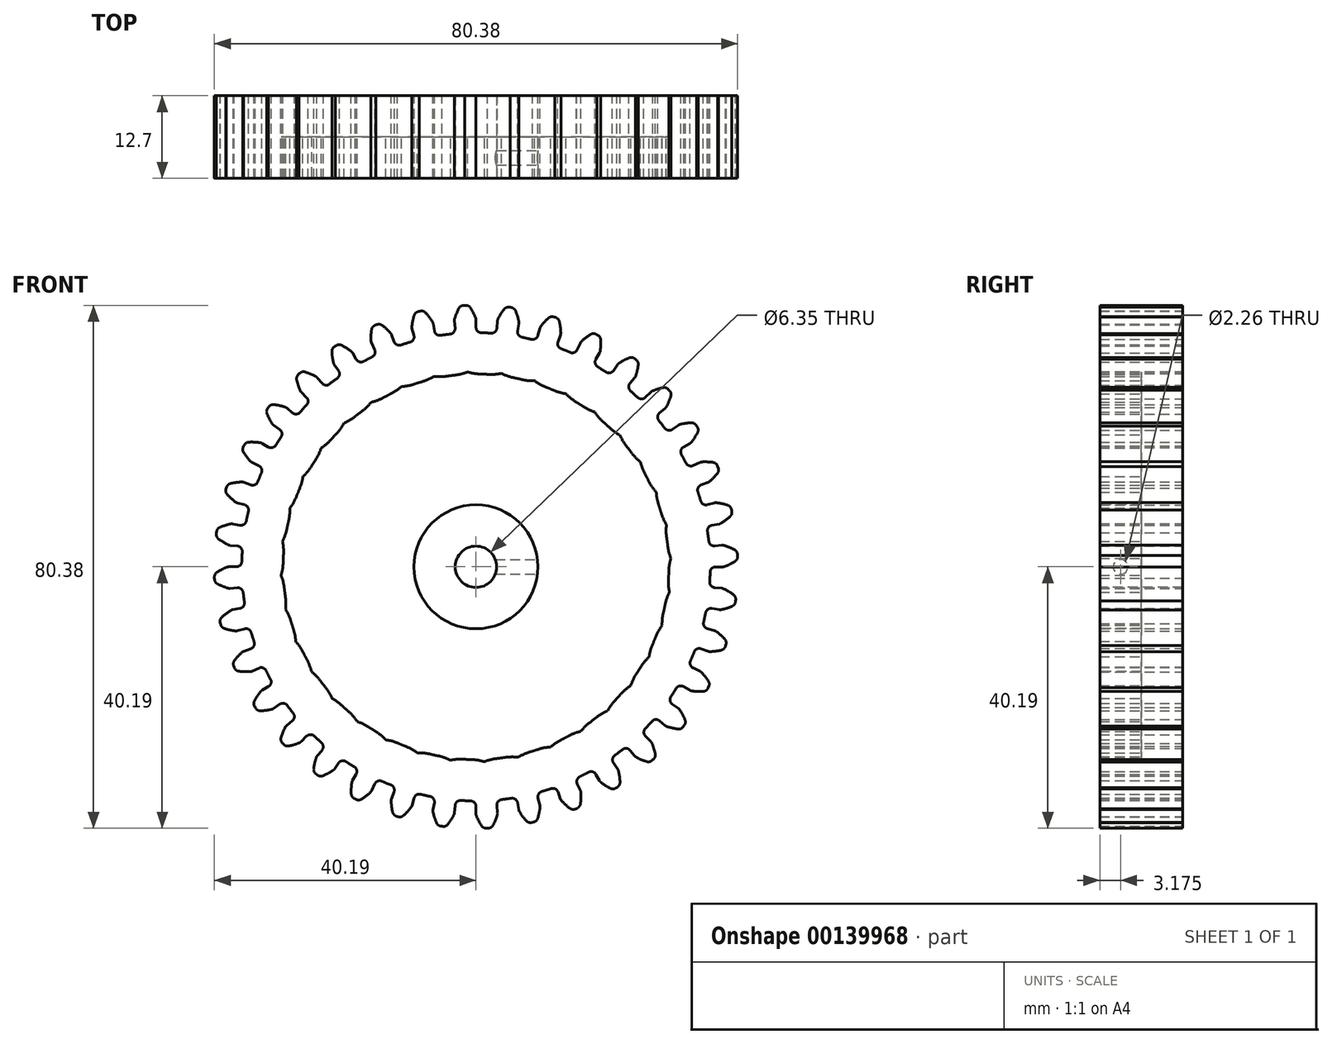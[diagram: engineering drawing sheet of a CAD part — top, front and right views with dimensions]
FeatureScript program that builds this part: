
annotation { "Feature Type Name" : "Feature", "Feature Type Description" : "" }
export const myFeature = defineFeature(function(context is Context, id is Id, definition is map)
    precondition{}
    {
        {
            var Q0;
            Q0=qCreatedBy(makeId("Front.planeOp"),FACE);
            var sketch = newSketch(context, id + "F0", { "sketchPlane" : qUnion([Q0])});
            skArc(sketch, "E0", {"start": v(-3.95, 35.77) * mm, "mid": v(-4.7, 35.68) * mm, "end": v(-5.44, 35.57) * mm});
            skArc(sketch, "E1.trimOffspring", {"start": v(-0.05, 38.26) * mm, "mid": v(-0.42, 39.05) * mm, "end": v(-0.85, 39.8) * mm});
            skLineSegment(sketch, "E2", {"start": v(0, 37.94) * mm, "end": v(0, 36.82) * mm});
            skLineSegment(sketch, "E3", {"start": v(-1.58, 40.19) * mm, "end": v(-1.75, 40.18) * mm});
            skLineSegment(sketch, "E4.MirrorCS", {"start": v(-1.93, 40.17) * mm, "end": v(-1.75, 40.18) * mm});
            skArc(sketch, "E5.MirrorCS", {"start": v(-3.28, 38.12) * mm, "mid": v(-2.99, 38.93) * mm, "end": v(-2.62, 39.72) * mm});
            skLineSegment(sketch, "E6.MirrorCS", {"start": v(-3.31, 37.8) * mm, "end": v(-3.21, 36.67) * mm});
            skPoint(sketch, "E7.visualSharp", {"position": v(-3.14, 35.85) * mm});
            skArc(sketch, "E7.filletArc", {"start": v(-3.95, 35.77) * mm, "mid": v(-3.4, 36.07) * mm, "end": v(-3.21, 36.67) * mm});
            skPoint(sketch, "E8.visualSharp", {"position": v(0, 35.98) * mm});
            skArc(sketch, "E8.filletArc", {"start": v(0, 36.82) * mm, "mid": v(0.24, 36.23) * mm, "end": v(0.82, 35.97) * mm});
            skPoint(sketch, "E9.visualSharp", {"position": v(0, 38.1) * mm});
            skArc(sketch, "E9.filletArc", {"start": v(0, 37.94) * mm, "mid": v(0, 38.1) * mm, "end": v(-0.05, 38.26) * mm});
            skPoint(sketch, "E10.visualSharp", {"position": v(-1.12, 40.2) * mm});
            skArc(sketch, "E10.filletArc", {"start": v(-0.85, 39.8) * mm, "mid": v(-1.16, 40.1) * mm, "end": v(-1.58, 40.19) * mm});
            skPoint(sketch, "E11.visualSharp", {"position": v(-3.33, 37.95) * mm});
            skArc(sketch, "E11.filletArc", {"start": v(-3.28, 38.12) * mm, "mid": v(-3.31, 37.96) * mm, "end": v(-3.31, 37.8) * mm});
            skPoint(sketch, "E12.visualSharp", {"position": v(-2.39, 40.15) * mm});
            skArc(sketch, "E12.filletArc", {"start": v(-1.93, 40.17) * mm, "mid": v(-2.34, 40.04) * mm, "end": v(-2.62, 39.72) * mm});
            skArc(sketch, "E13.1.0", {"start": v(-10.1, 34.54) * mm, "mid": v(-9.6, 34.93) * mm, "end": v(-9.53, 35.56) * mm});
            skLineSegment(sketch, "E13.1.1", {"start": v(-9.83, 36.64) * mm, "end": v(-9.53, 35.56) * mm});
            skArc(sketch, "E13.1.2", {"start": v(-9.85, 36.97) * mm, "mid": v(-9.7, 37.82) * mm, "end": v(-9.48, 38.66) * mm});
            skArc(sketch, "E13.1.3", {"start": v(-9.85, 36.97) * mm, "mid": v(-9.85, 36.8) * mm, "end": v(-9.83, 36.64) * mm});
            skArc(sketch, "E13.1.4", {"start": v(-8.88, 39.23) * mm, "mid": v(-9.25, 39.03) * mm, "end": v(-9.48, 38.66) * mm});
            skLineSegment(sketch, "E13.1.5", {"start": v(-8.53, 39.3) * mm, "end": v(-8.7, 39.27) * mm});
            skLineSegment(sketch, "E13.1.6", {"start": v(-8.88, 39.23) * mm, "end": v(-8.7, 39.27) * mm});
            skArc(sketch, "E13.1.7", {"start": v(-7.75, 39.05) * mm, "mid": v(-8.1, 39.28) * mm, "end": v(-8.53, 39.3) * mm});
            skArc(sketch, "E13.1.8", {"start": v(-6.7, 37.67) * mm, "mid": v(-7.19, 38.38) * mm, "end": v(-7.75, 39.05) * mm});
            skArc(sketch, "E13.1.9", {"start": v(-6.58, 37.36) * mm, "mid": v(-6.62, 37.52) * mm, "end": v(-6.7, 37.67) * mm});
            skLineSegment(sketch, "E13.1.10", {"start": v(-6.58, 37.36) * mm, "end": v(-6.39, 36.26) * mm});
            skArc(sketch, "E13.1.11", {"start": v(-6.39, 36.26) * mm, "mid": v(-6.05, 35.72) * mm, "end": v(-5.44, 35.57) * mm});
            skArc(sketch, "E13.2.0", {"start": v(-15.95, 32.26) * mm, "mid": v(-15.53, 32.73) * mm, "end": v(-15.56, 33.36) * mm});
            skLineSegment(sketch, "E13.2.1", {"start": v(-16.04, 34.38) * mm, "end": v(-15.56, 33.36) * mm});
            skArc(sketch, "E13.2.2", {"start": v(-16.12, 34.7) * mm, "mid": v(-16.13, 35.56) * mm, "end": v(-16.05, 36.43) * mm});
            skArc(sketch, "E13.2.3", {"start": v(-16.12, 34.7) * mm, "mid": v(-16.1, 34.53) * mm, "end": v(-16.04, 34.38) * mm});
            skArc(sketch, "E13.2.4", {"start": v(-15.55, 37.1) * mm, "mid": v(-15.89, 36.83) * mm, "end": v(-16.05, 36.43) * mm});
            skLineSegment(sketch, "E13.2.5", {"start": v(-15.23, 37.22) * mm, "end": v(-15.4, 37.16) * mm});
            skLineSegment(sketch, "E13.2.6", {"start": v(-15.55, 37.1) * mm, "end": v(-15.4, 37.16) * mm});
            skArc(sketch, "E13.2.7", {"start": v(-14.41, 37.11) * mm, "mid": v(-14.8, 37.28) * mm, "end": v(-15.23, 37.22) * mm});
            skArc(sketch, "E13.2.8", {"start": v(-13.13, 35.93) * mm, "mid": v(-13.75, 36.55) * mm, "end": v(-14.41, 37.11) * mm});
            skArc(sketch, "E13.2.9", {"start": v(-12.97, 35.65) * mm, "mid": v(-13.04, 35.8) * mm, "end": v(-13.13, 35.93) * mm});
            skLineSegment(sketch, "E13.2.10", {"start": v(-12.97, 35.65) * mm, "end": v(-12.59, 34.6) * mm});
            skArc(sketch, "E13.2.11", {"start": v(-12.59, 34.6) * mm, "mid": v(-12.16, 34.12) * mm, "end": v(-11.53, 34.09) * mm});
            skArc(sketch, "E13.3.0", {"start": v(-21.3, 29) * mm, "mid": v(-20.98, 29.54) * mm, "end": v(-21.12, 30.16) * mm});
            skLineSegment(sketch, "E13.3.1", {"start": v(-21.77, 31.07) * mm, "end": v(-21.12, 30.16) * mm});
            skArc(sketch, "E13.3.2", {"start": v(-21.9, 31.37) * mm, "mid": v(-22.06, 32.22) * mm, "end": v(-22.13, 33.09) * mm});
            skArc(sketch, "E13.3.3", {"start": v(-21.9, 31.37) * mm, "mid": v(-21.85, 31.21) * mm, "end": v(-21.77, 31.07) * mm});
            skArc(sketch, "E13.3.4", {"start": v(-21.76, 33.83) * mm, "mid": v(-22.04, 33.5) * mm, "end": v(-22.13, 33.09) * mm});
            skLineSegment(sketch, "E13.3.5", {"start": v(-21.46, 34.01) * mm, "end": v(-21.61, 33.92) * mm});
            skLineSegment(sketch, "E13.3.6", {"start": v(-21.76, 33.83) * mm, "end": v(-21.61, 33.92) * mm});
            skArc(sketch, "E13.3.7", {"start": v(-20.64, 34.04) * mm, "mid": v(-21.05, 34.14) * mm, "end": v(-21.46, 34.01) * mm});
            skArc(sketch, "E13.3.8", {"start": v(-19.17, 33.1) * mm, "mid": v(-19.88, 33.6) * mm, "end": v(-20.64, 34.04) * mm});
            skArc(sketch, "E13.3.9", {"start": v(-18.96, 32.86) * mm, "mid": v(-19.06, 33) * mm, "end": v(-19.17, 33.1) * mm});
            skLineSegment(sketch, "E13.3.10", {"start": v(-18.96, 32.86) * mm, "end": v(-18.4, 31.88) * mm});
            skArc(sketch, "E13.3.11", {"start": v(-18.4, 31.88) * mm, "mid": v(-17.9, 31.5) * mm, "end": v(-17.27, 31.57) * mm});
            skArc(sketch, "E13.4.0", {"start": v(-26.02, 24.86) * mm, "mid": v(-25.79, 25.45) * mm, "end": v(-26.03, 26.03) * mm});
            skLineSegment(sketch, "E13.4.1", {"start": v(-26.83, 26.82) * mm, "end": v(-26.03, 26.03) * mm});
            skArc(sketch, "E13.4.2", {"start": v(-27.01, 27.09) * mm, "mid": v(-27.32, 27.9) * mm, "end": v(-27.54, 28.74) * mm});
            skArc(sketch, "E13.4.3", {"start": v(-27.01, 27.09) * mm, "mid": v(-26.94, 26.95) * mm, "end": v(-26.83, 26.82) * mm});
            skArc(sketch, "E13.4.4", {"start": v(-27.3, 29.53) * mm, "mid": v(-27.53, 29.17) * mm, "end": v(-27.54, 28.74) * mm});
            skLineSegment(sketch, "E13.4.5", {"start": v(-27.04, 29.77) * mm, "end": v(-27.17, 29.65) * mm});
            skLineSegment(sketch, "E13.4.6", {"start": v(-27.3, 29.53) * mm, "end": v(-27.17, 29.65) * mm});
            skArc(sketch, "E13.4.7", {"start": v(-26.23, 29.94) * mm, "mid": v(-26.66, 29.96) * mm, "end": v(-27.04, 29.77) * mm});
            skArc(sketch, "E13.4.8", {"start": v(-24.63, 29.27) * mm, "mid": v(-25.42, 29.64) * mm, "end": v(-26.23, 29.94) * mm});
            skArc(sketch, "E13.4.9", {"start": v(-24.38, 29.07) * mm, "mid": v(-24.5, 29.18) * mm, "end": v(-24.63, 29.27) * mm});
            skLineSegment(sketch, "E13.4.10", {"start": v(-24.38, 29.07) * mm, "end": v(-23.66, 28.2) * mm});
            skArc(sketch, "E13.4.11", {"start": v(-23.66, 28.2) * mm, "mid": v(-23.1, 27.9) * mm, "end": v(-22.5, 28.09) * mm});
            skArc(sketch, "E13.5.0", {"start": v(-29.94, 19.96) * mm, "mid": v(-29.81, 20.58) * mm, "end": v(-30.16, 21.11) * mm});
            skLineSegment(sketch, "E13.5.1", {"start": v(-31.08, 21.75) * mm, "end": v(-30.16, 21.11) * mm});
            skArc(sketch, "E13.5.2", {"start": v(-31.3, 21.99) * mm, "mid": v(-31.75, 22.74) * mm, "end": v(-32.12, 23.52) * mm});
            skArc(sketch, "E13.5.3", {"start": v(-31.3, 21.99) * mm, "mid": v(-31.2, 21.86) * mm, "end": v(-31.08, 21.75) * mm});
            skArc(sketch, "E13.5.4", {"start": v(-32.01, 24.34) * mm, "mid": v(-32.17, 23.95) * mm, "end": v(-32.12, 23.52) * mm});
            skLineSegment(sketch, "E13.5.5", {"start": v(-31.8, 24.62) * mm, "end": v(-31.91, 24.49) * mm});
            skLineSegment(sketch, "E13.5.6", {"start": v(-32.01, 24.34) * mm, "end": v(-31.91, 24.49) * mm});
            skArc(sketch, "E13.5.7", {"start": v(-31.03, 24.93) * mm, "mid": v(-31.46, 24.88) * mm, "end": v(-31.8, 24.62) * mm});
            skArc(sketch, "E13.5.8", {"start": v(-29.34, 24.55) * mm, "mid": v(-30.18, 24.78) * mm, "end": v(-31.03, 24.93) * mm});
            skArc(sketch, "E13.5.9", {"start": v(-29.06, 24.4) * mm, "mid": v(-29.2, 24.49) * mm, "end": v(-29.34, 24.55) * mm});
            skLineSegment(sketch, "E13.5.10", {"start": v(-29.06, 24.4) * mm, "end": v(-28.2, 23.67) * mm});
            skArc(sketch, "E13.5.11", {"start": v(-28.2, 23.67) * mm, "mid": v(-27.6, 23.47) * mm, "end": v(-27.03, 23.75) * mm});
            skArc(sketch, "E13.6.0", {"start": v(-32.95, 14.46) * mm, "mid": v(-32.93, 15.1) * mm, "end": v(-33.37, 15.56) * mm});
            skLineSegment(sketch, "E13.6.1", {"start": v(-34.39, 16.03) * mm, "end": v(-33.37, 15.56) * mm});
            skArc(sketch, "E13.6.2", {"start": v(-34.65, 16.22) * mm, "mid": v(-35.21, 16.88) * mm, "end": v(-35.71, 17.59) * mm});
            skArc(sketch, "E13.6.3", {"start": v(-34.65, 16.22) * mm, "mid": v(-34.53, 16.1) * mm, "end": v(-34.39, 16.03) * mm});
            skArc(sketch, "E13.6.4", {"start": v(-35.76, 18.42) * mm, "mid": v(-35.84, 18) * mm, "end": v(-35.71, 17.59) * mm});
            skLineSegment(sketch, "E13.6.5", {"start": v(-35.6, 18.73) * mm, "end": v(-35.68, 18.57) * mm});
            skLineSegment(sketch, "E13.6.6", {"start": v(-35.76, 18.42) * mm, "end": v(-35.68, 18.57) * mm});
            skArc(sketch, "E13.6.7", {"start": v(-34.9, 19.17) * mm, "mid": v(-35.3, 19.04) * mm, "end": v(-35.6, 18.73) * mm});
            skArc(sketch, "E13.6.8", {"start": v(-33.16, 19.08) * mm, "mid": v(-34.02, 19.16) * mm, "end": v(-34.9, 19.17) * mm});
            skArc(sketch, "E13.6.9", {"start": v(-32.85, 18.98) * mm, "mid": v(-33, 19.04) * mm, "end": v(-33.16, 19.08) * mm});
            skLineSegment(sketch, "E13.6.10", {"start": v(-32.85, 18.98) * mm, "end": v(-31.88, 18.41) * mm});
            skArc(sketch, "E13.6.11", {"start": v(-31.88, 18.41) * mm, "mid": v(-31.25, 18.32) * mm, "end": v(-30.74, 18.7) * mm});
            skArc(sketch, "E13.7.0", {"start": v(-34.96, 8.52) * mm, "mid": v(-35.06, 9.14) * mm, "end": v(-35.56, 9.53) * mm});
            skLineSegment(sketch, "E13.7.1", {"start": v(-36.65, 9.81) * mm, "end": v(-35.56, 9.53) * mm});
            skArc(sketch, "E13.7.2", {"start": v(-36.94, 9.95) * mm, "mid": v(-37.6, 10.5) * mm, "end": v(-38.22, 11.12) * mm});
            skArc(sketch, "E13.7.3", {"start": v(-36.94, 9.95) * mm, "mid": v(-36.8, 9.87) * mm, "end": v(-36.65, 9.81) * mm});
            skArc(sketch, "E13.7.4", {"start": v(-38.41, 11.93) * mm, "mid": v(-38.42, 11.5) * mm, "end": v(-38.22, 11.12) * mm});
            skLineSegment(sketch, "E13.7.5", {"start": v(-38.3, 12.26) * mm, "end": v(-38.36, 12.1) * mm});
            skLineSegment(sketch, "E13.7.6", {"start": v(-38.41, 11.93) * mm, "end": v(-38.36, 12.1) * mm});
            skArc(sketch, "E13.7.7", {"start": v(-37.7, 12.81) * mm, "mid": v(-38.07, 12.62) * mm, "end": v(-38.3, 12.26) * mm});
            skArc(sketch, "E13.7.8", {"start": v(-35.97, 13.03) * mm, "mid": v(-36.83, 12.96) * mm, "end": v(-37.7, 12.81) * mm});
            skArc(sketch, "E13.7.9", {"start": v(-35.65, 12.98) * mm, "mid": v(-35.8, 13.02) * mm, "end": v(-35.97, 13.03) * mm});
            skLineSegment(sketch, "E13.7.10", {"start": v(-35.65, 12.98) * mm, "end": v(-34.6, 12.6) * mm});
            skArc(sketch, "E13.7.11", {"start": v(-34.6, 12.6) * mm, "mid": v(-33.96, 12.62) * mm, "end": v(-33.52, 13.08) * mm});
            skArc(sketch, "E13.8.0", {"start": v(-35.9, 2.32) * mm, "mid": v(-36.11, 2.92) * mm, "end": v(-36.68, 3.2) * mm});
            skLineSegment(sketch, "E13.8.1", {"start": v(-37.8, 3.3) * mm, "end": v(-36.68, 3.2) * mm});
            skArc(sketch, "E13.8.2", {"start": v(-38.1, 3.39) * mm, "mid": v(-38.86, 3.82) * mm, "end": v(-39.58, 4.31) * mm});
            skArc(sketch, "E13.8.3", {"start": v(-38.1, 3.39) * mm, "mid": v(-37.96, 3.33) * mm, "end": v(-37.8, 3.3) * mm});
            skArc(sketch, "E13.8.4", {"start": v(-39.9, 5.08) * mm, "mid": v(-39.84, 4.65) * mm, "end": v(-39.58, 4.31) * mm});
            skLineSegment(sketch, "E13.8.5", {"start": v(-39.85, 5.42) * mm, "end": v(-39.88, 5.25) * mm});
            skLineSegment(sketch, "E13.8.6", {"start": v(-39.9, 5.08) * mm, "end": v(-39.88, 5.25) * mm});
            skArc(sketch, "E13.8.7", {"start": v(-39.34, 6.08) * mm, "mid": v(-39.68, 5.82) * mm, "end": v(-39.85, 5.42) * mm});
            skArc(sketch, "E13.8.8", {"start": v(-37.68, 6.6) * mm, "mid": v(-38.53, 6.37) * mm, "end": v(-39.34, 6.08) * mm});
            skArc(sketch, "E13.8.9", {"start": v(-37.36, 6.6) * mm, "mid": v(-37.52, 6.6) * mm, "end": v(-37.68, 6.6) * mm});
            skLineSegment(sketch, "E13.8.10", {"start": v(-37.36, 6.6) * mm, "end": v(-36.26, 6.4) * mm});
            skArc(sketch, "E13.8.11", {"start": v(-36.26, 6.4) * mm, "mid": v(-35.64, 6.53) * mm, "end": v(-35.28, 7.06) * mm});
            skArc(sketch, "E13.9.0", {"start": v(-35.77, -3.95) * mm, "mid": v(-36.07, -3.4) * mm, "end": v(-36.67, -3.21) * mm});
            skLineSegment(sketch, "E13.9.1", {"start": v(-37.8, -3.31) * mm, "end": v(-36.67, -3.21) * mm});
            skArc(sketch, "E13.9.2", {"start": v(-38.12, -3.28) * mm, "mid": v(-38.93, -2.99) * mm, "end": v(-39.72, -2.62) * mm});
            skArc(sketch, "E13.9.3", {"start": v(-38.12, -3.28) * mm, "mid": v(-37.96, -3.31) * mm, "end": v(-37.8, -3.31) * mm});
            skArc(sketch, "E13.9.4", {"start": v(-40.17, -1.93) * mm, "mid": v(-40.04, -2.34) * mm, "end": v(-39.72, -2.62) * mm});
            skLineSegment(sketch, "E13.9.5", {"start": v(-40.19, -1.58) * mm, "end": v(-40.18, -1.75) * mm});
            skLineSegment(sketch, "E13.9.6", {"start": v(-40.17, -1.93) * mm, "end": v(-40.18, -1.75) * mm});
            skArc(sketch, "E13.9.7", {"start": v(-39.8, -0.85) * mm, "mid": v(-40.1, -1.16) * mm, "end": v(-40.19, -1.58) * mm});
            skArc(sketch, "E13.9.8", {"start": v(-38.26, -0.05) * mm, "mid": v(-39.05, -0.42) * mm, "end": v(-39.8, -0.85) * mm});
            skArc(sketch, "E13.9.9", {"start": v(-37.94, 0) * mm, "mid": v(-38.1, 0) * mm, "end": v(-38.26, -0.05) * mm});
            skLineSegment(sketch, "E13.9.10", {"start": v(-37.94, 0) * mm, "end": v(-36.82, 0) * mm});
            skArc(sketch, "E13.9.11", {"start": v(-36.82, 0) * mm, "mid": v(-36.23, 0.24) * mm, "end": v(-35.97, 0.82) * mm});
            skArc(sketch, "E13.10.0", {"start": v(-34.54, -10.1) * mm, "mid": v(-34.93, -9.6) * mm, "end": v(-35.56, -9.53) * mm});
            skLineSegment(sketch, "E13.10.1", {"start": v(-36.64, -9.83) * mm, "end": v(-35.56, -9.53) * mm});
            skArc(sketch, "E13.10.2", {"start": v(-36.97, -9.85) * mm, "mid": v(-37.82, -9.7) * mm, "end": v(-38.66, -9.48) * mm});
            skArc(sketch, "E13.10.3", {"start": v(-36.97, -9.85) * mm, "mid": v(-36.8, -9.85) * mm, "end": v(-36.64, -9.83) * mm});
            skArc(sketch, "E13.10.4", {"start": v(-39.23, -8.88) * mm, "mid": v(-39.03, -9.25) * mm, "end": v(-38.66, -9.48) * mm});
            skLineSegment(sketch, "E13.10.5", {"start": v(-39.3, -8.53) * mm, "end": v(-39.27, -8.7) * mm});
            skLineSegment(sketch, "E13.10.6", {"start": v(-39.23, -8.88) * mm, "end": v(-39.27, -8.7) * mm});
            skArc(sketch, "E13.10.7", {"start": v(-39.05, -7.75) * mm, "mid": v(-39.28, -8.1) * mm, "end": v(-39.3, -8.53) * mm});
            skArc(sketch, "E13.10.8", {"start": v(-37.67, -6.7) * mm, "mid": v(-38.38, -7.19) * mm, "end": v(-39.05, -7.75) * mm});
            skArc(sketch, "E13.10.9", {"start": v(-37.36, -6.58) * mm, "mid": v(-37.52, -6.62) * mm, "end": v(-37.67, -6.7) * mm});
            skLineSegment(sketch, "E13.10.10", {"start": v(-37.36, -6.58) * mm, "end": v(-36.26, -6.39) * mm});
            skArc(sketch, "E13.10.11", {"start": v(-36.26, -6.39) * mm, "mid": v(-35.72, -6.05) * mm, "end": v(-35.57, -5.44) * mm});
            skArc(sketch, "E13.11.0", {"start": v(-32.26, -15.95) * mm, "mid": v(-32.73, -15.53) * mm, "end": v(-33.36, -15.56) * mm});
            skLineSegment(sketch, "E13.11.1", {"start": v(-34.38, -16.04) * mm, "end": v(-33.36, -15.56) * mm});
            skArc(sketch, "E13.11.2", {"start": v(-34.7, -16.12) * mm, "mid": v(-35.56, -16.13) * mm, "end": v(-36.43, -16.05) * mm});
            skArc(sketch, "E13.11.3", {"start": v(-34.7, -16.12) * mm, "mid": v(-34.53, -16.1) * mm, "end": v(-34.38, -16.04) * mm});
            skArc(sketch, "E13.11.4", {"start": v(-37.1, -15.55) * mm, "mid": v(-36.83, -15.89) * mm, "end": v(-36.43, -16.05) * mm});
            skLineSegment(sketch, "E13.11.5", {"start": v(-37.22, -15.23) * mm, "end": v(-37.16, -15.4) * mm});
            skLineSegment(sketch, "E13.11.6", {"start": v(-37.1, -15.55) * mm, "end": v(-37.16, -15.4) * mm});
            skArc(sketch, "E13.11.7", {"start": v(-37.11, -14.41) * mm, "mid": v(-37.28, -14.8) * mm, "end": v(-37.22, -15.23) * mm});
            skArc(sketch, "E13.11.8", {"start": v(-35.93, -13.13) * mm, "mid": v(-36.55, -13.75) * mm, "end": v(-37.11, -14.41) * mm});
            skArc(sketch, "E13.11.9", {"start": v(-35.65, -12.97) * mm, "mid": v(-35.8, -13.04) * mm, "end": v(-35.93, -13.13) * mm});
            skLineSegment(sketch, "E13.11.10", {"start": v(-35.65, -12.97) * mm, "end": v(-34.6, -12.59) * mm});
            skArc(sketch, "E13.11.11", {"start": v(-34.6, -12.59) * mm, "mid": v(-34.12, -12.16) * mm, "end": v(-34.09, -11.53) * mm});
            skArc(sketch, "E13.12.0", {"start": v(-29, -21.3) * mm, "mid": v(-29.54, -20.98) * mm, "end": v(-30.16, -21.12) * mm});
            skLineSegment(sketch, "E13.12.1", {"start": v(-31.07, -21.77) * mm, "end": v(-30.16, -21.12) * mm});
            skArc(sketch, "E13.12.2", {"start": v(-31.37, -21.9) * mm, "mid": v(-32.22, -22.06) * mm, "end": v(-33.09, -22.13) * mm});
            skArc(sketch, "E13.12.3", {"start": v(-31.37, -21.9) * mm, "mid": v(-31.21, -21.85) * mm, "end": v(-31.07, -21.77) * mm});
            skArc(sketch, "E13.12.4", {"start": v(-33.83, -21.76) * mm, "mid": v(-33.5, -22.04) * mm, "end": v(-33.09, -22.13) * mm});
            skLineSegment(sketch, "E13.12.5", {"start": v(-34.01, -21.46) * mm, "end": v(-33.92, -21.61) * mm});
            skLineSegment(sketch, "E13.12.6", {"start": v(-33.83, -21.76) * mm, "end": v(-33.92, -21.61) * mm});
            skArc(sketch, "E13.12.7", {"start": v(-34.04, -20.64) * mm, "mid": v(-34.14, -21.05) * mm, "end": v(-34.01, -21.46) * mm});
            skArc(sketch, "E13.12.8", {"start": v(-33.1, -19.17) * mm, "mid": v(-33.6, -19.88) * mm, "end": v(-34.04, -20.64) * mm});
            skArc(sketch, "E13.12.9", {"start": v(-32.86, -18.96) * mm, "mid": v(-33, -19.06) * mm, "end": v(-33.1, -19.17) * mm});
            skLineSegment(sketch, "E13.12.10", {"start": v(-32.86, -18.96) * mm, "end": v(-31.88, -18.4) * mm});
            skArc(sketch, "E13.12.11", {"start": v(-31.88, -18.4) * mm, "mid": v(-31.5, -17.9) * mm, "end": v(-31.57, -17.27) * mm});
            skArc(sketch, "E13.13.0", {"start": v(-24.86, -26.02) * mm, "mid": v(-25.45, -25.79) * mm, "end": v(-26.03, -26.03) * mm});
            skLineSegment(sketch, "E13.13.1", {"start": v(-26.82, -26.83) * mm, "end": v(-26.03, -26.03) * mm});
            skArc(sketch, "E13.13.2", {"start": v(-27.09, -27.01) * mm, "mid": v(-27.9, -27.32) * mm, "end": v(-28.74, -27.54) * mm});
            skArc(sketch, "E13.13.3", {"start": v(-27.09, -27.01) * mm, "mid": v(-26.95, -26.94) * mm, "end": v(-26.82, -26.83) * mm});
            skArc(sketch, "E13.13.4", {"start": v(-29.53, -27.3) * mm, "mid": v(-29.17, -27.53) * mm, "end": v(-28.74, -27.54) * mm});
            skLineSegment(sketch, "E13.13.5", {"start": v(-29.77, -27.04) * mm, "end": v(-29.65, -27.17) * mm});
            skLineSegment(sketch, "E13.13.6", {"start": v(-29.53, -27.3) * mm, "end": v(-29.65, -27.17) * mm});
            skArc(sketch, "E13.13.7", {"start": v(-29.94, -26.23) * mm, "mid": v(-29.96, -26.66) * mm, "end": v(-29.77, -27.04) * mm});
            skArc(sketch, "E13.13.8", {"start": v(-29.27, -24.63) * mm, "mid": v(-29.64, -25.42) * mm, "end": v(-29.94, -26.23) * mm});
            skArc(sketch, "E13.13.9", {"start": v(-29.07, -24.38) * mm, "mid": v(-29.18, -24.5) * mm, "end": v(-29.27, -24.63) * mm});
            skLineSegment(sketch, "E13.13.10", {"start": v(-29.07, -24.38) * mm, "end": v(-28.2, -23.66) * mm});
            skArc(sketch, "E13.13.11", {"start": v(-28.2, -23.66) * mm, "mid": v(-27.9, -23.1) * mm, "end": v(-28.09, -22.5) * mm});
            skArc(sketch, "E13.14.0", {"start": v(-19.96, -29.94) * mm, "mid": v(-20.58, -29.81) * mm, "end": v(-21.11, -30.16) * mm});
            skLineSegment(sketch, "E13.14.1", {"start": v(-21.75, -31.08) * mm, "end": v(-21.11, -30.16) * mm});
            skArc(sketch, "E13.14.2", {"start": v(-21.99, -31.3) * mm, "mid": v(-22.74, -31.75) * mm, "end": v(-23.52, -32.12) * mm});
            skArc(sketch, "E13.14.3", {"start": v(-21.99, -31.3) * mm, "mid": v(-21.86, -31.2) * mm, "end": v(-21.75, -31.08) * mm});
            skArc(sketch, "E13.14.4", {"start": v(-24.34, -32.01) * mm, "mid": v(-23.95, -32.17) * mm, "end": v(-23.52, -32.12) * mm});
            skLineSegment(sketch, "E13.14.5", {"start": v(-24.62, -31.8) * mm, "end": v(-24.49, -31.91) * mm});
            skLineSegment(sketch, "E13.14.6", {"start": v(-24.34, -32.01) * mm, "end": v(-24.49, -31.91) * mm});
            skArc(sketch, "E13.14.7", {"start": v(-24.93, -31.03) * mm, "mid": v(-24.88, -31.46) * mm, "end": v(-24.62, -31.8) * mm});
            skArc(sketch, "E13.14.8", {"start": v(-24.55, -29.34) * mm, "mid": v(-24.78, -30.18) * mm, "end": v(-24.93, -31.03) * mm});
            skArc(sketch, "E13.14.9", {"start": v(-24.4, -29.06) * mm, "mid": v(-24.49, -29.2) * mm, "end": v(-24.55, -29.34) * mm});
            skLineSegment(sketch, "E13.14.10", {"start": v(-24.4, -29.06) * mm, "end": v(-23.67, -28.2) * mm});
            skArc(sketch, "E13.14.11", {"start": v(-23.67, -28.2) * mm, "mid": v(-23.47, -27.6) * mm, "end": v(-23.75, -27.03) * mm});
            skArc(sketch, "E13.15.0", {"start": v(-14.46, -32.95) * mm, "mid": v(-15.1, -32.93) * mm, "end": v(-15.56, -33.37) * mm});
            skLineSegment(sketch, "E13.15.1", {"start": v(-16.03, -34.39) * mm, "end": v(-15.56, -33.37) * mm});
            skArc(sketch, "E13.15.2", {"start": v(-16.22, -34.65) * mm, "mid": v(-16.88, -35.21) * mm, "end": v(-17.59, -35.71) * mm});
            skArc(sketch, "E13.15.3", {"start": v(-16.22, -34.65) * mm, "mid": v(-16.1, -34.53) * mm, "end": v(-16.03, -34.39) * mm});
            skArc(sketch, "E13.15.4", {"start": v(-18.42, -35.76) * mm, "mid": v(-18, -35.84) * mm, "end": v(-17.59, -35.71) * mm});
            skLineSegment(sketch, "E13.15.5", {"start": v(-18.73, -35.6) * mm, "end": v(-18.57, -35.68) * mm});
            skLineSegment(sketch, "E13.15.6", {"start": v(-18.42, -35.76) * mm, "end": v(-18.57, -35.68) * mm});
            skArc(sketch, "E13.15.7", {"start": v(-19.17, -34.9) * mm, "mid": v(-19.04, -35.3) * mm, "end": v(-18.73, -35.6) * mm});
            skArc(sketch, "E13.15.8", {"start": v(-19.08, -33.16) * mm, "mid": v(-19.16, -34.02) * mm, "end": v(-19.17, -34.9) * mm});
            skArc(sketch, "E13.15.9", {"start": v(-18.98, -32.85) * mm, "mid": v(-19.04, -33) * mm, "end": v(-19.08, -33.16) * mm});
            skLineSegment(sketch, "E13.15.10", {"start": v(-18.98, -32.85) * mm, "end": v(-18.41, -31.88) * mm});
            skArc(sketch, "E13.15.11", {"start": v(-18.41, -31.88) * mm, "mid": v(-18.32, -31.25) * mm, "end": v(-18.7, -30.74) * mm});
            skArc(sketch, "E13.16.0", {"start": v(-8.52, -34.96) * mm, "mid": v(-9.14, -35.06) * mm, "end": v(-9.53, -35.56) * mm});
            skLineSegment(sketch, "E13.16.1", {"start": v(-9.81, -36.65) * mm, "end": v(-9.53, -35.56) * mm});
            skArc(sketch, "E13.16.2", {"start": v(-9.95, -36.94) * mm, "mid": v(-10.5, -37.6) * mm, "end": v(-11.12, -38.22) * mm});
            skArc(sketch, "E13.16.3", {"start": v(-9.95, -36.94) * mm, "mid": v(-9.87, -36.8) * mm, "end": v(-9.81, -36.65) * mm});
            skArc(sketch, "E13.16.4", {"start": v(-11.93, -38.41) * mm, "mid": v(-11.5, -38.42) * mm, "end": v(-11.12, -38.22) * mm});
            skLineSegment(sketch, "E13.16.5", {"start": v(-12.26, -38.3) * mm, "end": v(-12.1, -38.36) * mm});
            skLineSegment(sketch, "E13.16.6", {"start": v(-11.93, -38.41) * mm, "end": v(-12.1, -38.36) * mm});
            skArc(sketch, "E13.16.7", {"start": v(-12.81, -37.7) * mm, "mid": v(-12.62, -38.07) * mm, "end": v(-12.26, -38.3) * mm});
            skArc(sketch, "E13.16.8", {"start": v(-13.03, -35.97) * mm, "mid": v(-12.96, -36.83) * mm, "end": v(-12.81, -37.7) * mm});
            skArc(sketch, "E13.16.9", {"start": v(-12.98, -35.65) * mm, "mid": v(-13.02, -35.8) * mm, "end": v(-13.03, -35.97) * mm});
            skLineSegment(sketch, "E13.16.10", {"start": v(-12.98, -35.65) * mm, "end": v(-12.6, -34.6) * mm});
            skArc(sketch, "E13.16.11", {"start": v(-12.6, -34.6) * mm, "mid": v(-12.62, -33.96) * mm, "end": v(-13.08, -33.52) * mm});
            skArc(sketch, "E13.17.0", {"start": v(-2.32, -35.9) * mm, "mid": v(-2.92, -36.11) * mm, "end": v(-3.2, -36.68) * mm});
            skLineSegment(sketch, "E13.17.1", {"start": v(-3.3, -37.8) * mm, "end": v(-3.2, -36.68) * mm});
            skArc(sketch, "E13.17.2", {"start": v(-3.39, -38.1) * mm, "mid": v(-3.82, -38.86) * mm, "end": v(-4.31, -39.58) * mm});
            skArc(sketch, "E13.17.3", {"start": v(-3.39, -38.1) * mm, "mid": v(-3.33, -37.96) * mm, "end": v(-3.3, -37.8) * mm});
            skArc(sketch, "E13.17.4", {"start": v(-5.08, -39.9) * mm, "mid": v(-4.65, -39.84) * mm, "end": v(-4.31, -39.58) * mm});
            skLineSegment(sketch, "E13.17.5", {"start": v(-5.42, -39.85) * mm, "end": v(-5.25, -39.88) * mm});
            skLineSegment(sketch, "E13.17.6", {"start": v(-5.08, -39.9) * mm, "end": v(-5.25, -39.88) * mm});
            skArc(sketch, "E13.17.7", {"start": v(-6.08, -39.34) * mm, "mid": v(-5.82, -39.68) * mm, "end": v(-5.42, -39.85) * mm});
            skArc(sketch, "E13.17.8", {"start": v(-6.6, -37.68) * mm, "mid": v(-6.37, -38.53) * mm, "end": v(-6.08, -39.34) * mm});
            skArc(sketch, "E13.17.9", {"start": v(-6.6, -37.36) * mm, "mid": v(-6.6, -37.52) * mm, "end": v(-6.6, -37.68) * mm});
            skLineSegment(sketch, "E13.17.10", {"start": v(-6.6, -37.36) * mm, "end": v(-6.4, -36.26) * mm});
            skArc(sketch, "E13.17.11", {"start": v(-6.4, -36.26) * mm, "mid": v(-6.53, -35.64) * mm, "end": v(-7.06, -35.28) * mm});
            skArc(sketch, "E13.18.0", {"start": v(3.95, -35.77) * mm, "mid": v(3.4, -36.07) * mm, "end": v(3.21, -36.67) * mm});
            skLineSegment(sketch, "E13.18.1", {"start": v(3.31, -37.8) * mm, "end": v(3.21, -36.67) * mm});
            skArc(sketch, "E13.18.2", {"start": v(3.28, -38.12) * mm, "mid": v(2.99, -38.93) * mm, "end": v(2.62, -39.72) * mm});
            skArc(sketch, "E13.18.3", {"start": v(3.28, -38.12) * mm, "mid": v(3.31, -37.96) * mm, "end": v(3.31, -37.8) * mm});
            skArc(sketch, "E13.18.4", {"start": v(1.93, -40.17) * mm, "mid": v(2.34, -40.04) * mm, "end": v(2.62, -39.72) * mm});
            skLineSegment(sketch, "E13.18.5", {"start": v(1.58, -40.19) * mm, "end": v(1.75, -40.18) * mm});
            skLineSegment(sketch, "E13.18.6", {"start": v(1.93, -40.17) * mm, "end": v(1.75, -40.18) * mm});
            skArc(sketch, "E13.18.7", {"start": v(0.85, -39.8) * mm, "mid": v(1.16, -40.1) * mm, "end": v(1.58, -40.19) * mm});
            skArc(sketch, "E13.18.8", {"start": v(0.05, -38.26) * mm, "mid": v(0.42, -39.05) * mm, "end": v(0.85, -39.8) * mm});
            skArc(sketch, "E13.18.9", {"start": v(0, -37.94) * mm, "mid": v(0, -38.1) * mm, "end": v(0.05, -38.26) * mm});
            skLineSegment(sketch, "E13.18.10", {"start": v(0, -37.94) * mm, "end": v(0, -36.82) * mm});
            skArc(sketch, "E13.18.11", {"start": v(0, -36.82) * mm, "mid": v(-0.24, -36.23) * mm, "end": v(-0.82, -35.97) * mm});
            skArc(sketch, "E13.19.0", {"start": v(10.1, -34.54) * mm, "mid": v(9.6, -34.93) * mm, "end": v(9.53, -35.56) * mm});
            skLineSegment(sketch, "E13.19.1", {"start": v(9.83, -36.64) * mm, "end": v(9.53, -35.56) * mm});
            skArc(sketch, "E13.19.2", {"start": v(9.85, -36.97) * mm, "mid": v(9.7, -37.82) * mm, "end": v(9.48, -38.66) * mm});
            skArc(sketch, "E13.19.3", {"start": v(9.85, -36.97) * mm, "mid": v(9.85, -36.8) * mm, "end": v(9.83, -36.64) * mm});
            skArc(sketch, "E13.19.4", {"start": v(8.88, -39.23) * mm, "mid": v(9.25, -39.03) * mm, "end": v(9.48, -38.66) * mm});
            skLineSegment(sketch, "E13.19.5", {"start": v(8.53, -39.3) * mm, "end": v(8.7, -39.27) * mm});
            skLineSegment(sketch, "E13.19.6", {"start": v(8.88, -39.23) * mm, "end": v(8.7, -39.27) * mm});
            skArc(sketch, "E13.19.7", {"start": v(7.75, -39.05) * mm, "mid": v(8.1, -39.28) * mm, "end": v(8.53, -39.3) * mm});
            skArc(sketch, "E13.19.8", {"start": v(6.7, -37.67) * mm, "mid": v(7.19, -38.38) * mm, "end": v(7.75, -39.05) * mm});
            skArc(sketch, "E13.19.9", {"start": v(6.58, -37.36) * mm, "mid": v(6.62, -37.52) * mm, "end": v(6.7, -37.67) * mm});
            skLineSegment(sketch, "E13.19.10", {"start": v(6.58, -37.36) * mm, "end": v(6.39, -36.26) * mm});
            skArc(sketch, "E13.19.11", {"start": v(6.39, -36.26) * mm, "mid": v(6.05, -35.72) * mm, "end": v(5.44, -35.57) * mm});
            skArc(sketch, "E13.20.0", {"start": v(15.95, -32.26) * mm, "mid": v(15.53, -32.73) * mm, "end": v(15.56, -33.36) * mm});
            skLineSegment(sketch, "E13.20.1", {"start": v(16.04, -34.38) * mm, "end": v(15.56, -33.36) * mm});
            skArc(sketch, "E13.20.2", {"start": v(16.12, -34.7) * mm, "mid": v(16.13, -35.56) * mm, "end": v(16.05, -36.43) * mm});
            skArc(sketch, "E13.20.3", {"start": v(16.12, -34.7) * mm, "mid": v(16.1, -34.53) * mm, "end": v(16.04, -34.38) * mm});
            skArc(sketch, "E13.20.4", {"start": v(15.55, -37.1) * mm, "mid": v(15.89, -36.83) * mm, "end": v(16.05, -36.43) * mm});
            skLineSegment(sketch, "E13.20.5", {"start": v(15.23, -37.22) * mm, "end": v(15.4, -37.16) * mm});
            skLineSegment(sketch, "E13.20.6", {"start": v(15.55, -37.1) * mm, "end": v(15.4, -37.16) * mm});
            skArc(sketch, "E13.20.7", {"start": v(14.41, -37.11) * mm, "mid": v(14.8, -37.28) * mm, "end": v(15.23, -37.22) * mm});
            skArc(sketch, "E13.20.8", {"start": v(13.13, -35.93) * mm, "mid": v(13.75, -36.55) * mm, "end": v(14.41, -37.11) * mm});
            skArc(sketch, "E13.20.9", {"start": v(12.97, -35.65) * mm, "mid": v(13.04, -35.8) * mm, "end": v(13.13, -35.93) * mm});
            skLineSegment(sketch, "E13.20.10", {"start": v(12.97, -35.65) * mm, "end": v(12.59, -34.6) * mm});
            skArc(sketch, "E13.20.11", {"start": v(12.59, -34.6) * mm, "mid": v(12.16, -34.12) * mm, "end": v(11.53, -34.09) * mm});
            skArc(sketch, "E13.21.0", {"start": v(21.3, -29) * mm, "mid": v(20.98, -29.54) * mm, "end": v(21.12, -30.16) * mm});
            skLineSegment(sketch, "E13.21.1", {"start": v(21.77, -31.07) * mm, "end": v(21.12, -30.16) * mm});
            skArc(sketch, "E13.21.2", {"start": v(21.9, -31.37) * mm, "mid": v(22.06, -32.22) * mm, "end": v(22.13, -33.09) * mm});
            skArc(sketch, "E13.21.3", {"start": v(21.9, -31.37) * mm, "mid": v(21.85, -31.21) * mm, "end": v(21.77, -31.07) * mm});
            skArc(sketch, "E13.21.4", {"start": v(21.76, -33.83) * mm, "mid": v(22.04, -33.5) * mm, "end": v(22.13, -33.09) * mm});
            skLineSegment(sketch, "E13.21.5", {"start": v(21.46, -34.01) * mm, "end": v(21.61, -33.92) * mm});
            skLineSegment(sketch, "E13.21.6", {"start": v(21.76, -33.83) * mm, "end": v(21.61, -33.92) * mm});
            skArc(sketch, "E13.21.7", {"start": v(20.64, -34.04) * mm, "mid": v(21.05, -34.14) * mm, "end": v(21.46, -34.01) * mm});
            skArc(sketch, "E13.21.8", {"start": v(19.17, -33.1) * mm, "mid": v(19.88, -33.6) * mm, "end": v(20.64, -34.04) * mm});
            skArc(sketch, "E13.21.9", {"start": v(18.96, -32.86) * mm, "mid": v(19.06, -33) * mm, "end": v(19.17, -33.1) * mm});
            skLineSegment(sketch, "E13.21.10", {"start": v(18.96, -32.86) * mm, "end": v(18.4, -31.88) * mm});
            skArc(sketch, "E13.21.11", {"start": v(18.4, -31.88) * mm, "mid": v(17.9, -31.5) * mm, "end": v(17.27, -31.57) * mm});
            skArc(sketch, "E13.22.0", {"start": v(26.02, -24.86) * mm, "mid": v(25.79, -25.45) * mm, "end": v(26.03, -26.03) * mm});
            skLineSegment(sketch, "E13.22.1", {"start": v(26.83, -26.82) * mm, "end": v(26.03, -26.03) * mm});
            skArc(sketch, "E13.22.2", {"start": v(27.01, -27.09) * mm, "mid": v(27.32, -27.9) * mm, "end": v(27.54, -28.74) * mm});
            skArc(sketch, "E13.22.3", {"start": v(27.01, -27.09) * mm, "mid": v(26.94, -26.95) * mm, "end": v(26.83, -26.82) * mm});
            skArc(sketch, "E13.22.4", {"start": v(27.3, -29.53) * mm, "mid": v(27.53, -29.17) * mm, "end": v(27.54, -28.74) * mm});
            skLineSegment(sketch, "E13.22.5", {"start": v(27.04, -29.77) * mm, "end": v(27.17, -29.65) * mm});
            skLineSegment(sketch, "E13.22.6", {"start": v(27.3, -29.53) * mm, "end": v(27.17, -29.65) * mm});
            skArc(sketch, "E13.22.7", {"start": v(26.23, -29.94) * mm, "mid": v(26.66, -29.96) * mm, "end": v(27.04, -29.77) * mm});
            skArc(sketch, "E13.22.8", {"start": v(24.63, -29.27) * mm, "mid": v(25.42, -29.64) * mm, "end": v(26.23, -29.94) * mm});
            skArc(sketch, "E13.22.9", {"start": v(24.38, -29.07) * mm, "mid": v(24.5, -29.18) * mm, "end": v(24.63, -29.27) * mm});
            skLineSegment(sketch, "E13.22.10", {"start": v(24.38, -29.07) * mm, "end": v(23.66, -28.2) * mm});
            skArc(sketch, "E13.22.11", {"start": v(23.66, -28.2) * mm, "mid": v(23.1, -27.9) * mm, "end": v(22.5, -28.09) * mm});
            skArc(sketch, "E13.23.0", {"start": v(29.94, -19.96) * mm, "mid": v(29.81, -20.58) * mm, "end": v(30.16, -21.11) * mm});
            skLineSegment(sketch, "E13.23.1", {"start": v(31.08, -21.75) * mm, "end": v(30.16, -21.11) * mm});
            skArc(sketch, "E13.23.2", {"start": v(31.3, -21.99) * mm, "mid": v(31.75, -22.74) * mm, "end": v(32.12, -23.52) * mm});
            skArc(sketch, "E13.23.3", {"start": v(31.3, -21.99) * mm, "mid": v(31.2, -21.86) * mm, "end": v(31.08, -21.75) * mm});
            skArc(sketch, "E13.23.4", {"start": v(32.01, -24.34) * mm, "mid": v(32.17, -23.95) * mm, "end": v(32.12, -23.52) * mm});
            skLineSegment(sketch, "E13.23.5", {"start": v(31.8, -24.62) * mm, "end": v(31.91, -24.49) * mm});
            skLineSegment(sketch, "E13.23.6", {"start": v(32.01, -24.34) * mm, "end": v(31.91, -24.49) * mm});
            skArc(sketch, "E13.23.7", {"start": v(31.03, -24.93) * mm, "mid": v(31.46, -24.88) * mm, "end": v(31.8, -24.62) * mm});
            skArc(sketch, "E13.23.8", {"start": v(29.34, -24.55) * mm, "mid": v(30.18, -24.78) * mm, "end": v(31.03, -24.93) * mm});
            skArc(sketch, "E13.23.9", {"start": v(29.06, -24.4) * mm, "mid": v(29.2, -24.49) * mm, "end": v(29.34, -24.55) * mm});
            skLineSegment(sketch, "E13.23.10", {"start": v(29.06, -24.4) * mm, "end": v(28.2, -23.67) * mm});
            skArc(sketch, "E13.23.11", {"start": v(28.2, -23.67) * mm, "mid": v(27.6, -23.47) * mm, "end": v(27.03, -23.75) * mm});
            skArc(sketch, "E13.24.0", {"start": v(32.95, -14.46) * mm, "mid": v(32.93, -15.1) * mm, "end": v(33.37, -15.56) * mm});
            skLineSegment(sketch, "E13.24.1", {"start": v(34.39, -16.03) * mm, "end": v(33.37, -15.56) * mm});
            skArc(sketch, "E13.24.2", {"start": v(34.65, -16.22) * mm, "mid": v(35.21, -16.88) * mm, "end": v(35.71, -17.59) * mm});
            skArc(sketch, "E13.24.3", {"start": v(34.65, -16.22) * mm, "mid": v(34.53, -16.1) * mm, "end": v(34.39, -16.03) * mm});
            skArc(sketch, "E13.24.4", {"start": v(35.76, -18.42) * mm, "mid": v(35.84, -18) * mm, "end": v(35.71, -17.59) * mm});
            skLineSegment(sketch, "E13.24.5", {"start": v(35.6, -18.73) * mm, "end": v(35.68, -18.57) * mm});
            skLineSegment(sketch, "E13.24.6", {"start": v(35.76, -18.42) * mm, "end": v(35.68, -18.57) * mm});
            skArc(sketch, "E13.24.7", {"start": v(34.9, -19.17) * mm, "mid": v(35.3, -19.04) * mm, "end": v(35.6, -18.73) * mm});
            skArc(sketch, "E13.24.8", {"start": v(33.16, -19.08) * mm, "mid": v(34.02, -19.16) * mm, "end": v(34.9, -19.17) * mm});
            skArc(sketch, "E13.24.9", {"start": v(32.85, -18.98) * mm, "mid": v(33, -19.04) * mm, "end": v(33.16, -19.08) * mm});
            skLineSegment(sketch, "E13.24.10", {"start": v(32.85, -18.98) * mm, "end": v(31.88, -18.41) * mm});
            skArc(sketch, "E13.24.11", {"start": v(31.88, -18.41) * mm, "mid": v(31.25, -18.32) * mm, "end": v(30.74, -18.7) * mm});
            skArc(sketch, "E13.25.0", {"start": v(34.96, -8.52) * mm, "mid": v(35.06, -9.14) * mm, "end": v(35.56, -9.53) * mm});
            skLineSegment(sketch, "E13.25.1", {"start": v(36.65, -9.81) * mm, "end": v(35.56, -9.53) * mm});
            skArc(sketch, "E13.25.2", {"start": v(36.94, -9.95) * mm, "mid": v(37.6, -10.5) * mm, "end": v(38.22, -11.12) * mm});
            skArc(sketch, "E13.25.3", {"start": v(36.94, -9.95) * mm, "mid": v(36.8, -9.87) * mm, "end": v(36.65, -9.81) * mm});
            skArc(sketch, "E13.25.4", {"start": v(38.41, -11.93) * mm, "mid": v(38.42, -11.5) * mm, "end": v(38.22, -11.12) * mm});
            skLineSegment(sketch, "E13.25.5", {"start": v(38.3, -12.26) * mm, "end": v(38.36, -12.1) * mm});
            skLineSegment(sketch, "E13.25.6", {"start": v(38.41, -11.93) * mm, "end": v(38.36, -12.1) * mm});
            skArc(sketch, "E13.25.7", {"start": v(37.7, -12.81) * mm, "mid": v(38.07, -12.62) * mm, "end": v(38.3, -12.26) * mm});
            skArc(sketch, "E13.25.8", {"start": v(35.97, -13.03) * mm, "mid": v(36.83, -12.96) * mm, "end": v(37.7, -12.81) * mm});
            skArc(sketch, "E13.25.9", {"start": v(35.65, -12.98) * mm, "mid": v(35.8, -13.02) * mm, "end": v(35.97, -13.03) * mm});
            skLineSegment(sketch, "E13.25.10", {"start": v(35.65, -12.98) * mm, "end": v(34.6, -12.6) * mm});
            skArc(sketch, "E13.25.11", {"start": v(34.6, -12.6) * mm, "mid": v(33.96, -12.62) * mm, "end": v(33.52, -13.08) * mm});
            skArc(sketch, "E13.26.0", {"start": v(35.9, -2.32) * mm, "mid": v(36.11, -2.92) * mm, "end": v(36.68, -3.2) * mm});
            skLineSegment(sketch, "E13.26.1", {"start": v(37.8, -3.3) * mm, "end": v(36.68, -3.2) * mm});
            skArc(sketch, "E13.26.2", {"start": v(38.1, -3.39) * mm, "mid": v(38.86, -3.82) * mm, "end": v(39.58, -4.31) * mm});
            skArc(sketch, "E13.26.3", {"start": v(38.1, -3.39) * mm, "mid": v(37.96, -3.33) * mm, "end": v(37.8, -3.3) * mm});
            skArc(sketch, "E13.26.4", {"start": v(39.9, -5.08) * mm, "mid": v(39.84, -4.65) * mm, "end": v(39.58, -4.31) * mm});
            skLineSegment(sketch, "E13.26.5", {"start": v(39.85, -5.42) * mm, "end": v(39.88, -5.25) * mm});
            skLineSegment(sketch, "E13.26.6", {"start": v(39.9, -5.08) * mm, "end": v(39.88, -5.25) * mm});
            skArc(sketch, "E13.26.7", {"start": v(39.34, -6.08) * mm, "mid": v(39.68, -5.82) * mm, "end": v(39.85, -5.42) * mm});
            skArc(sketch, "E13.26.8", {"start": v(37.68, -6.6) * mm, "mid": v(38.53, -6.37) * mm, "end": v(39.34, -6.08) * mm});
            skArc(sketch, "E13.26.9", {"start": v(37.36, -6.6) * mm, "mid": v(37.52, -6.6) * mm, "end": v(37.68, -6.6) * mm});
            skLineSegment(sketch, "E13.26.10", {"start": v(37.36, -6.6) * mm, "end": v(36.26, -6.4) * mm});
            skArc(sketch, "E13.26.11", {"start": v(36.26, -6.4) * mm, "mid": v(35.64, -6.53) * mm, "end": v(35.28, -7.06) * mm});
            skArc(sketch, "E13.27.0", {"start": v(35.77, 3.95) * mm, "mid": v(36.07, 3.4) * mm, "end": v(36.67, 3.21) * mm});
            skLineSegment(sketch, "E13.27.1", {"start": v(37.8, 3.31) * mm, "end": v(36.67, 3.21) * mm});
            skArc(sketch, "E13.27.2", {"start": v(38.12, 3.28) * mm, "mid": v(38.93, 2.99) * mm, "end": v(39.72, 2.62) * mm});
            skArc(sketch, "E13.27.3", {"start": v(38.12, 3.28) * mm, "mid": v(37.96, 3.31) * mm, "end": v(37.8, 3.31) * mm});
            skArc(sketch, "E13.27.4", {"start": v(40.17, 1.93) * mm, "mid": v(40.04, 2.34) * mm, "end": v(39.72, 2.62) * mm});
            skLineSegment(sketch, "E13.27.5", {"start": v(40.19, 1.58) * mm, "end": v(40.18, 1.75) * mm});
            skLineSegment(sketch, "E13.27.6", {"start": v(40.17, 1.93) * mm, "end": v(40.18, 1.75) * mm});
            skArc(sketch, "E13.27.7", {"start": v(39.8, 0.85) * mm, "mid": v(40.1, 1.16) * mm, "end": v(40.19, 1.58) * mm});
            skArc(sketch, "E13.27.8", {"start": v(38.26, 0.05) * mm, "mid": v(39.05, 0.42) * mm, "end": v(39.8, 0.85) * mm});
            skArc(sketch, "E13.27.9", {"start": v(37.94, 0) * mm, "mid": v(38.1, 0) * mm, "end": v(38.26, 0.05) * mm});
            skLineSegment(sketch, "E13.27.10", {"start": v(37.94, 0) * mm, "end": v(36.82, 0) * mm});
            skArc(sketch, "E13.27.11", {"start": v(36.82, 0) * mm, "mid": v(36.23, -0.24) * mm, "end": v(35.97, -0.82) * mm});
            skArc(sketch, "E13.28.0", {"start": v(34.54, 10.1) * mm, "mid": v(34.93, 9.6) * mm, "end": v(35.56, 9.53) * mm});
            skLineSegment(sketch, "E13.28.1", {"start": v(36.64, 9.83) * mm, "end": v(35.56, 9.53) * mm});
            skArc(sketch, "E13.28.2", {"start": v(36.97, 9.85) * mm, "mid": v(37.82, 9.7) * mm, "end": v(38.66, 9.48) * mm});
            skArc(sketch, "E13.28.3", {"start": v(36.97, 9.85) * mm, "mid": v(36.8, 9.85) * mm, "end": v(36.64, 9.83) * mm});
            skArc(sketch, "E13.28.4", {"start": v(39.23, 8.88) * mm, "mid": v(39.03, 9.25) * mm, "end": v(38.66, 9.48) * mm});
            skLineSegment(sketch, "E13.28.5", {"start": v(39.3, 8.53) * mm, "end": v(39.27, 8.7) * mm});
            skLineSegment(sketch, "E13.28.6", {"start": v(39.23, 8.88) * mm, "end": v(39.27, 8.7) * mm});
            skArc(sketch, "E13.28.7", {"start": v(39.05, 7.75) * mm, "mid": v(39.28, 8.1) * mm, "end": v(39.3, 8.53) * mm});
            skArc(sketch, "E13.28.8", {"start": v(37.67, 6.7) * mm, "mid": v(38.38, 7.19) * mm, "end": v(39.05, 7.75) * mm});
            skArc(sketch, "E13.28.9", {"start": v(37.36, 6.58) * mm, "mid": v(37.52, 6.62) * mm, "end": v(37.67, 6.7) * mm});
            skLineSegment(sketch, "E13.28.10", {"start": v(37.36, 6.58) * mm, "end": v(36.26, 6.39) * mm});
            skArc(sketch, "E13.28.11", {"start": v(36.26, 6.39) * mm, "mid": v(35.72, 6.05) * mm, "end": v(35.57, 5.44) * mm});
            skArc(sketch, "E13.29.0", {"start": v(32.26, 15.95) * mm, "mid": v(32.73, 15.53) * mm, "end": v(33.36, 15.56) * mm});
            skLineSegment(sketch, "E13.29.1", {"start": v(34.38, 16.04) * mm, "end": v(33.36, 15.56) * mm});
            skArc(sketch, "E13.29.2", {"start": v(34.7, 16.12) * mm, "mid": v(35.56, 16.13) * mm, "end": v(36.43, 16.05) * mm});
            skArc(sketch, "E13.29.3", {"start": v(34.7, 16.12) * mm, "mid": v(34.53, 16.1) * mm, "end": v(34.38, 16.04) * mm});
            skArc(sketch, "E13.29.4", {"start": v(37.1, 15.55) * mm, "mid": v(36.83, 15.89) * mm, "end": v(36.43, 16.05) * mm});
            skLineSegment(sketch, "E13.29.5", {"start": v(37.22, 15.23) * mm, "end": v(37.16, 15.4) * mm});
            skLineSegment(sketch, "E13.29.6", {"start": v(37.1, 15.55) * mm, "end": v(37.16, 15.4) * mm});
            skArc(sketch, "E13.29.7", {"start": v(37.11, 14.41) * mm, "mid": v(37.28, 14.8) * mm, "end": v(37.22, 15.23) * mm});
            skArc(sketch, "E13.29.8", {"start": v(35.93, 13.13) * mm, "mid": v(36.55, 13.75) * mm, "end": v(37.11, 14.41) * mm});
            skArc(sketch, "E13.29.9", {"start": v(35.65, 12.97) * mm, "mid": v(35.8, 13.04) * mm, "end": v(35.93, 13.13) * mm});
            skLineSegment(sketch, "E13.29.10", {"start": v(35.65, 12.97) * mm, "end": v(34.6, 12.59) * mm});
            skArc(sketch, "E13.29.11", {"start": v(34.6, 12.59) * mm, "mid": v(34.12, 12.16) * mm, "end": v(34.09, 11.53) * mm});
            skArc(sketch, "E13.30.0", {"start": v(29, 21.3) * mm, "mid": v(29.54, 20.98) * mm, "end": v(30.16, 21.12) * mm});
            skLineSegment(sketch, "E13.30.1", {"start": v(31.07, 21.77) * mm, "end": v(30.16, 21.12) * mm});
            skArc(sketch, "E13.30.2", {"start": v(31.37, 21.9) * mm, "mid": v(32.22, 22.06) * mm, "end": v(33.09, 22.13) * mm});
            skArc(sketch, "E13.30.3", {"start": v(31.37, 21.9) * mm, "mid": v(31.21, 21.85) * mm, "end": v(31.07, 21.77) * mm});
            skArc(sketch, "E13.30.4", {"start": v(33.83, 21.76) * mm, "mid": v(33.5, 22.04) * mm, "end": v(33.09, 22.13) * mm});
            skLineSegment(sketch, "E13.30.5", {"start": v(34.01, 21.46) * mm, "end": v(33.92, 21.61) * mm});
            skLineSegment(sketch, "E13.30.6", {"start": v(33.83, 21.76) * mm, "end": v(33.92, 21.61) * mm});
            skArc(sketch, "E13.30.7", {"start": v(34.04, 20.64) * mm, "mid": v(34.14, 21.05) * mm, "end": v(34.01, 21.46) * mm});
            skArc(sketch, "E13.30.8", {"start": v(33.1, 19.17) * mm, "mid": v(33.6, 19.88) * mm, "end": v(34.04, 20.64) * mm});
            skArc(sketch, "E13.30.9", {"start": v(32.86, 18.96) * mm, "mid": v(33, 19.06) * mm, "end": v(33.1, 19.17) * mm});
            skLineSegment(sketch, "E13.30.10", {"start": v(32.86, 18.96) * mm, "end": v(31.88, 18.4) * mm});
            skArc(sketch, "E13.30.11", {"start": v(31.88, 18.4) * mm, "mid": v(31.5, 17.9) * mm, "end": v(31.57, 17.27) * mm});
            skArc(sketch, "E13.31.0", {"start": v(24.86, 26.02) * mm, "mid": v(25.45, 25.79) * mm, "end": v(26.03, 26.03) * mm});
            skLineSegment(sketch, "E13.31.1", {"start": v(26.82, 26.83) * mm, "end": v(26.03, 26.03) * mm});
            skArc(sketch, "E13.31.2", {"start": v(27.09, 27.01) * mm, "mid": v(27.9, 27.32) * mm, "end": v(28.74, 27.54) * mm});
            skArc(sketch, "E13.31.3", {"start": v(27.09, 27.01) * mm, "mid": v(26.95, 26.94) * mm, "end": v(26.82, 26.83) * mm});
            skArc(sketch, "E13.31.4", {"start": v(29.53, 27.3) * mm, "mid": v(29.17, 27.53) * mm, "end": v(28.74, 27.54) * mm});
            skLineSegment(sketch, "E13.31.5", {"start": v(29.77, 27.04) * mm, "end": v(29.65, 27.17) * mm});
            skLineSegment(sketch, "E13.31.6", {"start": v(29.53, 27.3) * mm, "end": v(29.65, 27.17) * mm});
            skArc(sketch, "E13.31.7", {"start": v(29.94, 26.23) * mm, "mid": v(29.96, 26.66) * mm, "end": v(29.77, 27.04) * mm});
            skArc(sketch, "E13.31.8", {"start": v(29.27, 24.63) * mm, "mid": v(29.64, 25.42) * mm, "end": v(29.94, 26.23) * mm});
            skArc(sketch, "E13.31.9", {"start": v(29.07, 24.38) * mm, "mid": v(29.18, 24.5) * mm, "end": v(29.27, 24.63) * mm});
            skLineSegment(sketch, "E13.31.10", {"start": v(29.07, 24.38) * mm, "end": v(28.2, 23.66) * mm});
            skArc(sketch, "E13.31.11", {"start": v(28.2, 23.66) * mm, "mid": v(27.9, 23.1) * mm, "end": v(28.09, 22.5) * mm});
            skArc(sketch, "E13.32.0", {"start": v(19.96, 29.94) * mm, "mid": v(20.58, 29.81) * mm, "end": v(21.11, 30.16) * mm});
            skLineSegment(sketch, "E13.32.1", {"start": v(21.75, 31.08) * mm, "end": v(21.11, 30.16) * mm});
            skArc(sketch, "E13.32.2", {"start": v(21.99, 31.3) * mm, "mid": v(22.74, 31.75) * mm, "end": v(23.52, 32.12) * mm});
            skArc(sketch, "E13.32.3", {"start": v(21.99, 31.3) * mm, "mid": v(21.86, 31.2) * mm, "end": v(21.75, 31.08) * mm});
            skArc(sketch, "E13.32.4", {"start": v(24.34, 32.01) * mm, "mid": v(23.95, 32.17) * mm, "end": v(23.52, 32.12) * mm});
            skLineSegment(sketch, "E13.32.5", {"start": v(24.62, 31.8) * mm, "end": v(24.49, 31.91) * mm});
            skLineSegment(sketch, "E13.32.6", {"start": v(24.34, 32.01) * mm, "end": v(24.49, 31.91) * mm});
            skArc(sketch, "E13.32.7", {"start": v(24.93, 31.03) * mm, "mid": v(24.88, 31.46) * mm, "end": v(24.62, 31.8) * mm});
            skArc(sketch, "E13.32.8", {"start": v(24.55, 29.34) * mm, "mid": v(24.78, 30.18) * mm, "end": v(24.93, 31.03) * mm});
            skArc(sketch, "E13.32.9", {"start": v(24.4, 29.06) * mm, "mid": v(24.49, 29.2) * mm, "end": v(24.55, 29.34) * mm});
            skLineSegment(sketch, "E13.32.10", {"start": v(24.4, 29.06) * mm, "end": v(23.67, 28.2) * mm});
            skArc(sketch, "E13.32.11", {"start": v(23.67, 28.2) * mm, "mid": v(23.47, 27.6) * mm, "end": v(23.75, 27.03) * mm});
            skArc(sketch, "E13.33.0", {"start": v(14.46, 32.95) * mm, "mid": v(15.1, 32.93) * mm, "end": v(15.56, 33.37) * mm});
            skLineSegment(sketch, "E13.33.1", {"start": v(16.03, 34.39) * mm, "end": v(15.56, 33.37) * mm});
            skArc(sketch, "E13.33.2", {"start": v(16.22, 34.65) * mm, "mid": v(16.88, 35.21) * mm, "end": v(17.59, 35.71) * mm});
            skArc(sketch, "E13.33.3", {"start": v(16.22, 34.65) * mm, "mid": v(16.1, 34.53) * mm, "end": v(16.03, 34.39) * mm});
            skArc(sketch, "E13.33.4", {"start": v(18.42, 35.76) * mm, "mid": v(18, 35.84) * mm, "end": v(17.59, 35.71) * mm});
            skLineSegment(sketch, "E13.33.5", {"start": v(18.73, 35.6) * mm, "end": v(18.57, 35.68) * mm});
            skLineSegment(sketch, "E13.33.6", {"start": v(18.42, 35.76) * mm, "end": v(18.57, 35.68) * mm});
            skArc(sketch, "E13.33.7", {"start": v(19.17, 34.9) * mm, "mid": v(19.04, 35.3) * mm, "end": v(18.73, 35.6) * mm});
            skArc(sketch, "E13.33.8", {"start": v(19.08, 33.16) * mm, "mid": v(19.16, 34.02) * mm, "end": v(19.17, 34.9) * mm});
            skArc(sketch, "E13.33.9", {"start": v(18.98, 32.85) * mm, "mid": v(19.04, 33) * mm, "end": v(19.08, 33.16) * mm});
            skLineSegment(sketch, "E13.33.10", {"start": v(18.98, 32.85) * mm, "end": v(18.41, 31.88) * mm});
            skArc(sketch, "E13.33.11", {"start": v(18.41, 31.88) * mm, "mid": v(18.32, 31.25) * mm, "end": v(18.7, 30.74) * mm});
            skArc(sketch, "E13.34.0", {"start": v(8.52, 34.96) * mm, "mid": v(9.14, 35.06) * mm, "end": v(9.53, 35.56) * mm});
            skLineSegment(sketch, "E13.34.1", {"start": v(9.81, 36.65) * mm, "end": v(9.53, 35.56) * mm});
            skArc(sketch, "E13.34.2", {"start": v(9.95, 36.94) * mm, "mid": v(10.5, 37.6) * mm, "end": v(11.12, 38.22) * mm});
            skArc(sketch, "E13.34.3", {"start": v(9.95, 36.94) * mm, "mid": v(9.87, 36.8) * mm, "end": v(9.81, 36.65) * mm});
            skArc(sketch, "E13.34.4", {"start": v(11.93, 38.41) * mm, "mid": v(11.5, 38.42) * mm, "end": v(11.12, 38.22) * mm});
            skLineSegment(sketch, "E13.34.5", {"start": v(12.26, 38.3) * mm, "end": v(12.1, 38.36) * mm});
            skLineSegment(sketch, "E13.34.6", {"start": v(11.93, 38.41) * mm, "end": v(12.1, 38.36) * mm});
            skArc(sketch, "E13.34.7", {"start": v(12.81, 37.7) * mm, "mid": v(12.62, 38.07) * mm, "end": v(12.26, 38.3) * mm});
            skArc(sketch, "E13.34.8", {"start": v(13.03, 35.97) * mm, "mid": v(12.96, 36.83) * mm, "end": v(12.81, 37.7) * mm});
            skArc(sketch, "E13.34.9", {"start": v(12.98, 35.65) * mm, "mid": v(13.02, 35.8) * mm, "end": v(13.03, 35.97) * mm});
            skLineSegment(sketch, "E13.34.10", {"start": v(12.98, 35.65) * mm, "end": v(12.6, 34.6) * mm});
            skArc(sketch, "E13.34.11", {"start": v(12.6, 34.6) * mm, "mid": v(12.62, 33.96) * mm, "end": v(13.08, 33.52) * mm});
            skArc(sketch, "E13.35.0", {"start": v(2.32, 35.9) * mm, "mid": v(2.92, 36.11) * mm, "end": v(3.2, 36.68) * mm});
            skLineSegment(sketch, "E13.35.1", {"start": v(3.3, 37.8) * mm, "end": v(3.2, 36.68) * mm});
            skArc(sketch, "E13.35.2", {"start": v(3.39, 38.1) * mm, "mid": v(3.82, 38.86) * mm, "end": v(4.31, 39.58) * mm});
            skArc(sketch, "E13.35.3", {"start": v(3.39, 38.1) * mm, "mid": v(3.33, 37.96) * mm, "end": v(3.3, 37.8) * mm});
            skArc(sketch, "E13.35.4", {"start": v(5.08, 39.9) * mm, "mid": v(4.65, 39.84) * mm, "end": v(4.31, 39.58) * mm});
            skLineSegment(sketch, "E13.35.5", {"start": v(5.42, 39.85) * mm, "end": v(5.25, 39.88) * mm});
            skLineSegment(sketch, "E13.35.6", {"start": v(5.08, 39.9) * mm, "end": v(5.25, 39.88) * mm});
            skArc(sketch, "E13.35.7", {"start": v(6.08, 39.34) * mm, "mid": v(5.82, 39.68) * mm, "end": v(5.42, 39.85) * mm});
            skArc(sketch, "E13.35.8", {"start": v(6.6, 37.68) * mm, "mid": v(6.37, 38.53) * mm, "end": v(6.08, 39.34) * mm});
            skArc(sketch, "E13.35.9", {"start": v(6.6, 37.36) * mm, "mid": v(6.6, 37.52) * mm, "end": v(6.6, 37.68) * mm});
            skLineSegment(sketch, "E13.35.10", {"start": v(6.6, 37.36) * mm, "end": v(6.4, 36.26) * mm});
            skArc(sketch, "E13.35.11", {"start": v(6.4, 36.26) * mm, "mid": v(6.53, 35.64) * mm, "end": v(7.06, 35.28) * mm});
            skArc(sketch, "E14.trimOffspring", {"start": v(2.32, 35.9) * mm, "mid": v(1.57, 35.95) * mm, "end": v(0.82, 35.97) * mm});
            skArc(sketch, "E15.trimOffspring", {"start": v(8.52, 34.96) * mm, "mid": v(7.79, 35.13) * mm, "end": v(7.06, 35.28) * mm});
            skArc(sketch, "E16.trimOffspring", {"start": v(14.46, 32.95) * mm, "mid": v(13.77, 33.24) * mm, "end": v(13.08, 33.52) * mm});
            skArc(sketch, "E17.trimOffspring", {"start": v(-32.95, 14.46) * mm, "mid": v(-33.24, 13.77) * mm, "end": v(-33.52, 13.08) * mm});
            skArc(sketch, "E18.trimOffspring", {"start": v(-29.94, 19.96) * mm, "mid": v(-30.35, 19.33) * mm, "end": v(-30.74, 18.7) * mm});
            skArc(sketch, "E19.trimOffspring", {"start": v(-26.02, 24.86) * mm, "mid": v(-26.53, 24.3) * mm, "end": v(-27.03, 23.75) * mm});
            skArc(sketch, "E20.trimOffspring", {"start": v(-21.3, 29) * mm, "mid": v(-21.9, 28.55) * mm, "end": v(-22.5, 28.09) * mm});
            skArc(sketch, "E21.trimOffspring", {"start": v(-10.1, 34.54) * mm, "mid": v(-10.82, 34.32) * mm, "end": v(-11.53, 34.09) * mm});
            skArc(sketch, "E22.trimOffspring", {"start": v(-15.95, 32.26) * mm, "mid": v(-16.62, 31.92) * mm, "end": v(-17.27, 31.57) * mm});
            skArc(sketch, "E23.trimOffspring", {"start": v(-34.96, 8.52) * mm, "mid": v(-35.13, 7.79) * mm, "end": v(-35.28, 7.06) * mm});
            skArc(sketch, "E24.trimOffspring", {"start": v(-35.9, 2.32) * mm, "mid": v(-35.95, 1.57) * mm, "end": v(-35.97, 0.82) * mm});
            skArc(sketch, "E25.trimOffspring", {"start": v(-35.77, -3.95) * mm, "mid": v(-35.68, -4.7) * mm, "end": v(-35.57, -5.44) * mm});
            skArc(sketch, "E26.trimOffspring", {"start": v(-34.54, -10.1) * mm, "mid": v(-34.32, -10.82) * mm, "end": v(-34.09, -11.53) * mm});
            skArc(sketch, "E27.trimOffspring", {"start": v(-32.26, -15.95) * mm, "mid": v(-31.92, -16.62) * mm, "end": v(-31.57, -17.27) * mm});
            skArc(sketch, "E28.trimOffspring", {"start": v(19.96, 29.94) * mm, "mid": v(19.33, 30.35) * mm, "end": v(18.7, 30.74) * mm});
            skArc(sketch, "E29.trimOffspring", {"start": v(24.86, 26.02) * mm, "mid": v(24.3, 26.53) * mm, "end": v(23.75, 27.03) * mm});
            skArc(sketch, "E30.trimOffspring", {"start": v(29, 21.3) * mm, "mid": v(28.55, 21.9) * mm, "end": v(28.09, 22.5) * mm});
            skArc(sketch, "E31.trimOffspring", {"start": v(32.26, 15.95) * mm, "mid": v(31.92, 16.62) * mm, "end": v(31.57, 17.27) * mm});
            skArc(sketch, "E32.trimOffspring", {"start": v(34.54, 10.1) * mm, "mid": v(34.32, 10.82) * mm, "end": v(34.09, 11.53) * mm});
            skArc(sketch, "E33.trimOffspring", {"start": v(35.77, 3.95) * mm, "mid": v(35.68, 4.7) * mm, "end": v(35.57, 5.44) * mm});
            skArc(sketch, "E34.trimOffspring", {"start": v(35.9, -2.32) * mm, "mid": v(35.95, -1.57) * mm, "end": v(35.97, -0.82) * mm});
            skArc(sketch, "E35.trimOffspring", {"start": v(34.96, -8.52) * mm, "mid": v(35.13, -7.79) * mm, "end": v(35.28, -7.06) * mm});
            skArc(sketch, "E36.trimOffspring", {"start": v(32.95, -14.46) * mm, "mid": v(33.24, -13.77) * mm, "end": v(33.52, -13.08) * mm});
            skArc(sketch, "E37.trimOffspring", {"start": v(29.94, -19.96) * mm, "mid": v(30.35, -19.33) * mm, "end": v(30.74, -18.7) * mm});
            skArc(sketch, "E38.trimOffspring", {"start": v(26.02, -24.86) * mm, "mid": v(26.53, -24.3) * mm, "end": v(27.03, -23.75) * mm});
            skArc(sketch, "E39.trimOffspring", {"start": v(21.3, -29) * mm, "mid": v(21.9, -28.55) * mm, "end": v(22.5, -28.09) * mm});
            skArc(sketch, "E40.trimOffspring", {"start": v(15.95, -32.26) * mm, "mid": v(16.62, -31.92) * mm, "end": v(17.27, -31.57) * mm});
            skArc(sketch, "E41.trimOffspring", {"start": v(-2.32, -35.9) * mm, "mid": v(-1.57, -35.95) * mm, "end": v(-0.82, -35.97) * mm});
            skArc(sketch, "E42.trimOffspring", {"start": v(-8.52, -34.96) * mm, "mid": v(-7.79, -35.13) * mm, "end": v(-7.06, -35.28) * mm});
            skArc(sketch, "E43.trimOffspring", {"start": v(-14.46, -32.95) * mm, "mid": v(-13.77, -33.24) * mm, "end": v(-13.08, -33.52) * mm});
            skArc(sketch, "E44.trimOffspring", {"start": v(-19.96, -29.94) * mm, "mid": v(-19.33, -30.35) * mm, "end": v(-18.7, -30.74) * mm});
            skArc(sketch, "E45.trimOffspring", {"start": v(-24.86, -26.02) * mm, "mid": v(-24.3, -26.53) * mm, "end": v(-23.75, -27.03) * mm});
            skArc(sketch, "E46.trimOffspring", {"start": v(-29, -21.3) * mm, "mid": v(-28.55, -21.9) * mm, "end": v(-28.09, -22.5) * mm});
            skArc(sketch, "E47.trimOffspring", {"start": v(3.95, -35.77) * mm, "mid": v(4.7, -35.68) * mm, "end": v(5.44, -35.57) * mm});
            skArc(sketch, "E48.trimOffspring", {"start": v(10.1, -34.54) * mm, "mid": v(10.82, -34.32) * mm, "end": v(11.53, -34.09) * mm});
            skSolve(sketch);
        }
        {
            var Q0;
            Q0 = qSketchRegion(id + "F0", true);
            extrude(context, id + "F1", {"entities" : qUnion([Q0]), "depth" : 12.7 * mm});
        }
        {
            var Q0;
            Q0=makeQuery(id+"F1.opExtrude","CAP_FACE",FACE,{"disambiguationData":[OSD([sQuery(id+"F0.wireOp",EDGE,"E0"),sQuery(id+"F0.wireOp",EDGE,"E1.trimOffspring"),sQuery(id+"F0.wireOp",EDGE,"E2"),sQuery(id+"F0.wireOp",EDGE,"E3"),sQuery(id+"F0.wireOp",EDGE,"E4.MirrorCS"),sQuery(id+"F0.wireOp",EDGE,"E5.MirrorCS"),sQuery(id+"F0.wireOp",EDGE,"E6.MirrorCS"),sQuery(id+"F0.wireOp",EDGE,"E7.filletArc"),sQuery(id+"F0.wireOp",EDGE,"E8.filletArc"),sQuery(id+"F0.wireOp",EDGE,"E9.filletArc"),sQuery(id+"F0.wireOp",EDGE,"E10.filletArc"),sQuery(id+"F0.wireOp",EDGE,"E11.filletArc"),sQuery(id+"F0.wireOp",EDGE,"E12.filletArc"),sQuery(id+"F0.wireOp",EDGE,"E13.1.0"),sQuery(id+"F0.wireOp",EDGE,"E13.1.1"),sQuery(id+"F0.wireOp",EDGE,"E13.1.2"),sQuery(id+"F0.wireOp",EDGE,"E13.1.3"),sQuery(id+"F0.wireOp",EDGE,"E13.1.4"),sQuery(id+"F0.wireOp",EDGE,"E13.1.5"),sQuery(id+"F0.wireOp",EDGE,"E13.1.6"),sQuery(id+"F0.wireOp",EDGE,"E13.1.7"),sQuery(id+"F0.wireOp",EDGE,"E13.1.8"),sQuery(id+"F0.wireOp",EDGE,"E13.1.9"),sQuery(id+"F0.wireOp",EDGE,"E13.1.10"),sQuery(id+"F0.wireOp",EDGE,"E13.1.11"),sQuery(id+"F0.wireOp",EDGE,"E13.2.0"),sQuery(id+"F0.wireOp",EDGE,"E13.2.1"),sQuery(id+"F0.wireOp",EDGE,"E13.2.2"),sQuery(id+"F0.wireOp",EDGE,"E13.2.3"),sQuery(id+"F0.wireOp",EDGE,"E13.2.4"),sQuery(id+"F0.wireOp",EDGE,"E13.2.5"),sQuery(id+"F0.wireOp",EDGE,"E13.2.6"),sQuery(id+"F0.wireOp",EDGE,"E13.2.7"),sQuery(id+"F0.wireOp",EDGE,"E13.2.8"),sQuery(id+"F0.wireOp",EDGE,"E13.2.9"),sQuery(id+"F0.wireOp",EDGE,"E13.2.10"),sQuery(id+"F0.wireOp",EDGE,"E13.2.11"),sQuery(id+"F0.wireOp",EDGE,"E13.3.0"),sQuery(id+"F0.wireOp",EDGE,"E13.3.1"),sQuery(id+"F0.wireOp",EDGE,"E13.3.2"),sQuery(id+"F0.wireOp",EDGE,"E13.3.3"),sQuery(id+"F0.wireOp",EDGE,"E13.3.4"),sQuery(id+"F0.wireOp",EDGE,"E13.3.5"),sQuery(id+"F0.wireOp",EDGE,"E13.3.6"),sQuery(id+"F0.wireOp",EDGE,"E13.3.7"),sQuery(id+"F0.wireOp",EDGE,"E13.3.8"),sQuery(id+"F0.wireOp",EDGE,"E13.3.9"),sQuery(id+"F0.wireOp",EDGE,"E13.3.10"),sQuery(id+"F0.wireOp",EDGE,"E13.3.11"),sQuery(id+"F0.wireOp",EDGE,"E13.4.0"),sQuery(id+"F0.wireOp",EDGE,"E13.4.1"),sQuery(id+"F0.wireOp",EDGE,"E13.4.2"),sQuery(id+"F0.wireOp",EDGE,"E13.4.3"),sQuery(id+"F0.wireOp",EDGE,"E13.4.4"),sQuery(id+"F0.wireOp",EDGE,"E13.4.5"),sQuery(id+"F0.wireOp",EDGE,"E13.4.6"),sQuery(id+"F0.wireOp",EDGE,"E13.4.7"),sQuery(id+"F0.wireOp",EDGE,"E13.4.8"),sQuery(id+"F0.wireOp",EDGE,"E13.4.9"),sQuery(id+"F0.wireOp",EDGE,"E13.4.10"),sQuery(id+"F0.wireOp",EDGE,"E13.4.11"),sQuery(id+"F0.wireOp",EDGE,"E13.5.0"),sQuery(id+"F0.wireOp",EDGE,"E13.5.1"),sQuery(id+"F0.wireOp",EDGE,"E13.5.2"),sQuery(id+"F0.wireOp",EDGE,"E13.5.3"),sQuery(id+"F0.wireOp",EDGE,"E13.5.4"),sQuery(id+"F0.wireOp",EDGE,"E13.5.5"),sQuery(id+"F0.wireOp",EDGE,"E13.5.6"),sQuery(id+"F0.wireOp",EDGE,"E13.5.7"),sQuery(id+"F0.wireOp",EDGE,"E13.5.8"),sQuery(id+"F0.wireOp",EDGE,"E13.5.9"),sQuery(id+"F0.wireOp",EDGE,"E13.5.10"),sQuery(id+"F0.wireOp",EDGE,"E13.5.11"),sQuery(id+"F0.wireOp",EDGE,"E13.6.0"),sQuery(id+"F0.wireOp",EDGE,"E13.6.1"),sQuery(id+"F0.wireOp",EDGE,"E13.6.2"),sQuery(id+"F0.wireOp",EDGE,"E13.6.3"),sQuery(id+"F0.wireOp",EDGE,"E13.6.4"),sQuery(id+"F0.wireOp",EDGE,"E13.6.5"),sQuery(id+"F0.wireOp",EDGE,"E13.6.6"),sQuery(id+"F0.wireOp",EDGE,"E13.6.7"),sQuery(id+"F0.wireOp",EDGE,"E13.6.8"),sQuery(id+"F0.wireOp",EDGE,"E13.6.9"),sQuery(id+"F0.wireOp",EDGE,"E13.6.10"),sQuery(id+"F0.wireOp",EDGE,"E13.6.11"),sQuery(id+"F0.wireOp",EDGE,"E13.7.0"),sQuery(id+"F0.wireOp",EDGE,"E13.7.1"),sQuery(id+"F0.wireOp",EDGE,"E13.7.2"),sQuery(id+"F0.wireOp",EDGE,"E13.7.3"),sQuery(id+"F0.wireOp",EDGE,"E13.7.4"),sQuery(id+"F0.wireOp",EDGE,"E13.7.5"),sQuery(id+"F0.wireOp",EDGE,"E13.7.6"),sQuery(id+"F0.wireOp",EDGE,"E13.7.7"),sQuery(id+"F0.wireOp",EDGE,"E13.7.8"),sQuery(id+"F0.wireOp",EDGE,"E13.7.9"),sQuery(id+"F0.wireOp",EDGE,"E13.7.10"),sQuery(id+"F0.wireOp",EDGE,"E13.7.11"),sQuery(id+"F0.wireOp",EDGE,"E13.8.0"),sQuery(id+"F0.wireOp",EDGE,"E13.8.1"),sQuery(id+"F0.wireOp",EDGE,"E13.8.2"),sQuery(id+"F0.wireOp",EDGE,"E13.8.3"),sQuery(id+"F0.wireOp",EDGE,"E13.8.4"),sQuery(id+"F0.wireOp",EDGE,"E13.8.5"),sQuery(id+"F0.wireOp",EDGE,"E13.8.6"),sQuery(id+"F0.wireOp",EDGE,"E13.8.7"),sQuery(id+"F0.wireOp",EDGE,"E13.8.8"),sQuery(id+"F0.wireOp",EDGE,"E13.8.9"),sQuery(id+"F0.wireOp",EDGE,"E13.8.10"),sQuery(id+"F0.wireOp",EDGE,"E13.8.11"),sQuery(id+"F0.wireOp",EDGE,"E13.9.0"),sQuery(id+"F0.wireOp",EDGE,"E13.9.1"),sQuery(id+"F0.wireOp",EDGE,"E13.9.2"),sQuery(id+"F0.wireOp",EDGE,"E13.9.3"),sQuery(id+"F0.wireOp",EDGE,"E13.9.4"),sQuery(id+"F0.wireOp",EDGE,"E13.9.5"),sQuery(id+"F0.wireOp",EDGE,"E13.9.6"),sQuery(id+"F0.wireOp",EDGE,"E13.9.7"),sQuery(id+"F0.wireOp",EDGE,"E13.9.8"),sQuery(id+"F0.wireOp",EDGE,"E13.9.9"),sQuery(id+"F0.wireOp",EDGE,"E13.9.10"),sQuery(id+"F0.wireOp",EDGE,"E13.9.11"),sQuery(id+"F0.wireOp",EDGE,"E13.10.0"),sQuery(id+"F0.wireOp",EDGE,"E13.10.1"),sQuery(id+"F0.wireOp",EDGE,"E13.10.2"),sQuery(id+"F0.wireOp",EDGE,"E13.10.3"),sQuery(id+"F0.wireOp",EDGE,"E13.10.4"),sQuery(id+"F0.wireOp",EDGE,"E13.10.5"),sQuery(id+"F0.wireOp",EDGE,"E13.10.6"),sQuery(id+"F0.wireOp",EDGE,"E13.10.7"),sQuery(id+"F0.wireOp",EDGE,"E13.10.8"),sQuery(id+"F0.wireOp",EDGE,"E13.10.9"),sQuery(id+"F0.wireOp",EDGE,"E13.10.10"),sQuery(id+"F0.wireOp",EDGE,"E13.10.11"),sQuery(id+"F0.wireOp",EDGE,"E13.11.0"),sQuery(id+"F0.wireOp",EDGE,"E13.11.1"),sQuery(id+"F0.wireOp",EDGE,"E13.11.2"),sQuery(id+"F0.wireOp",EDGE,"E13.11.3"),sQuery(id+"F0.wireOp",EDGE,"E13.11.4"),sQuery(id+"F0.wireOp",EDGE,"E13.11.5"),sQuery(id+"F0.wireOp",EDGE,"E13.11.6"),sQuery(id+"F0.wireOp",EDGE,"E13.11.7"),sQuery(id+"F0.wireOp",EDGE,"E13.11.8"),sQuery(id+"F0.wireOp",EDGE,"E13.11.9"),sQuery(id+"F0.wireOp",EDGE,"E13.11.10"),sQuery(id+"F0.wireOp",EDGE,"E13.11.11"),sQuery(id+"F0.wireOp",EDGE,"E13.12.0"),sQuery(id+"F0.wireOp",EDGE,"E13.12.1"),sQuery(id+"F0.wireOp",EDGE,"E13.12.2"),sQuery(id+"F0.wireOp",EDGE,"E13.12.3"),sQuery(id+"F0.wireOp",EDGE,"E13.12.4"),sQuery(id+"F0.wireOp",EDGE,"E13.12.5"),sQuery(id+"F0.wireOp",EDGE,"E13.12.6"),sQuery(id+"F0.wireOp",EDGE,"E13.12.7"),sQuery(id+"F0.wireOp",EDGE,"E13.12.8"),sQuery(id+"F0.wireOp",EDGE,"E13.12.9"),sQuery(id+"F0.wireOp",EDGE,"E13.12.10"),sQuery(id+"F0.wireOp",EDGE,"E13.12.11"),sQuery(id+"F0.wireOp",EDGE,"E13.13.0"),sQuery(id+"F0.wireOp",EDGE,"E13.13.1"),sQuery(id+"F0.wireOp",EDGE,"E13.13.2"),sQuery(id+"F0.wireOp",EDGE,"E13.13.3"),sQuery(id+"F0.wireOp",EDGE,"E13.13.4"),sQuery(id+"F0.wireOp",EDGE,"E13.13.5"),sQuery(id+"F0.wireOp",EDGE,"E13.13.6"),sQuery(id+"F0.wireOp",EDGE,"E13.13.7"),sQuery(id+"F0.wireOp",EDGE,"E13.13.8"),sQuery(id+"F0.wireOp",EDGE,"E13.13.9"),sQuery(id+"F0.wireOp",EDGE,"E13.13.10"),sQuery(id+"F0.wireOp",EDGE,"E13.13.11"),sQuery(id+"F0.wireOp",EDGE,"E13.14.0"),sQuery(id+"F0.wireOp",EDGE,"E13.14.1"),sQuery(id+"F0.wireOp",EDGE,"E13.14.2"),sQuery(id+"F0.wireOp",EDGE,"E13.14.3"),sQuery(id+"F0.wireOp",EDGE,"E13.14.4"),sQuery(id+"F0.wireOp",EDGE,"E13.14.5"),sQuery(id+"F0.wireOp",EDGE,"E13.14.6"),sQuery(id+"F0.wireOp",EDGE,"E13.14.7"),sQuery(id+"F0.wireOp",EDGE,"E13.14.8"),sQuery(id+"F0.wireOp",EDGE,"E13.14.9"),sQuery(id+"F0.wireOp",EDGE,"E13.14.10"),sQuery(id+"F0.wireOp",EDGE,"E13.14.11"),sQuery(id+"F0.wireOp",EDGE,"E13.15.0"),sQuery(id+"F0.wireOp",EDGE,"E13.15.1"),sQuery(id+"F0.wireOp",EDGE,"E13.15.2"),sQuery(id+"F0.wireOp",EDGE,"E13.15.3"),sQuery(id+"F0.wireOp",EDGE,"E13.15.4"),sQuery(id+"F0.wireOp",EDGE,"E13.15.5"),sQuery(id+"F0.wireOp",EDGE,"E13.15.6"),sQuery(id+"F0.wireOp",EDGE,"E13.15.7"),sQuery(id+"F0.wireOp",EDGE,"E13.15.8"),sQuery(id+"F0.wireOp",EDGE,"E13.15.9"),sQuery(id+"F0.wireOp",EDGE,"E13.15.10"),sQuery(id+"F0.wireOp",EDGE,"E13.15.11"),sQuery(id+"F0.wireOp",EDGE,"E13.16.0"),sQuery(id+"F0.wireOp",EDGE,"E13.16.1"),sQuery(id+"F0.wireOp",EDGE,"E13.16.2"),sQuery(id+"F0.wireOp",EDGE,"E13.16.3"),sQuery(id+"F0.wireOp",EDGE,"E13.16.4"),sQuery(id+"F0.wireOp",EDGE,"E13.16.5"),sQuery(id+"F0.wireOp",EDGE,"E13.16.6"),sQuery(id+"F0.wireOp",EDGE,"E13.16.7"),sQuery(id+"F0.wireOp",EDGE,"E13.16.8"),sQuery(id+"F0.wireOp",EDGE,"E13.16.9"),sQuery(id+"F0.wireOp",EDGE,"E13.16.10"),sQuery(id+"F0.wireOp",EDGE,"E13.16.11"),sQuery(id+"F0.wireOp",EDGE,"E13.17.0"),sQuery(id+"F0.wireOp",EDGE,"E13.17.1"),sQuery(id+"F0.wireOp",EDGE,"E13.17.2"),sQuery(id+"F0.wireOp",EDGE,"E13.17.3"),sQuery(id+"F0.wireOp",EDGE,"E13.17.4"),sQuery(id+"F0.wireOp",EDGE,"E13.17.5"),sQuery(id+"F0.wireOp",EDGE,"E13.17.6"),sQuery(id+"F0.wireOp",EDGE,"E13.17.7"),sQuery(id+"F0.wireOp",EDGE,"E13.17.8"),sQuery(id+"F0.wireOp",EDGE,"E13.17.9"),sQuery(id+"F0.wireOp",EDGE,"E13.17.10"),sQuery(id+"F0.wireOp",EDGE,"E13.17.11"),sQuery(id+"F0.wireOp",EDGE,"E13.18.0"),sQuery(id+"F0.wireOp",EDGE,"E13.18.1"),sQuery(id+"F0.wireOp",EDGE,"E13.18.2"),sQuery(id+"F0.wireOp",EDGE,"E13.18.3"),sQuery(id+"F0.wireOp",EDGE,"E13.18.4"),sQuery(id+"F0.wireOp",EDGE,"E13.18.5"),sQuery(id+"F0.wireOp",EDGE,"E13.18.6"),sQuery(id+"F0.wireOp",EDGE,"E13.18.7"),sQuery(id+"F0.wireOp",EDGE,"E13.18.8"),sQuery(id+"F0.wireOp",EDGE,"E13.18.9"),sQuery(id+"F0.wireOp",EDGE,"E13.18.10"),sQuery(id+"F0.wireOp",EDGE,"E13.18.11"),sQuery(id+"F0.wireOp",EDGE,"E13.19.0"),sQuery(id+"F0.wireOp",EDGE,"E13.19.1"),sQuery(id+"F0.wireOp",EDGE,"E13.19.2"),sQuery(id+"F0.wireOp",EDGE,"E13.19.3"),sQuery(id+"F0.wireOp",EDGE,"E13.19.4"),sQuery(id+"F0.wireOp",EDGE,"E13.19.5"),sQuery(id+"F0.wireOp",EDGE,"E13.19.6"),sQuery(id+"F0.wireOp",EDGE,"E13.19.7"),sQuery(id+"F0.wireOp",EDGE,"E13.19.8"),sQuery(id+"F0.wireOp",EDGE,"E13.19.9"),sQuery(id+"F0.wireOp",EDGE,"E13.19.10"),sQuery(id+"F0.wireOp",EDGE,"E13.19.11"),sQuery(id+"F0.wireOp",EDGE,"E13.20.0"),sQuery(id+"F0.wireOp",EDGE,"E13.20.1"),sQuery(id+"F0.wireOp",EDGE,"E13.20.2"),sQuery(id+"F0.wireOp",EDGE,"E13.20.3"),sQuery(id+"F0.wireOp",EDGE,"E13.20.4"),sQuery(id+"F0.wireOp",EDGE,"E13.20.5"),sQuery(id+"F0.wireOp",EDGE,"E13.20.6"),sQuery(id+"F0.wireOp",EDGE,"E13.20.7"),sQuery(id+"F0.wireOp",EDGE,"E13.20.8"),sQuery(id+"F0.wireOp",EDGE,"E13.20.9"),sQuery(id+"F0.wireOp",EDGE,"E13.20.10"),sQuery(id+"F0.wireOp",EDGE,"E13.20.11"),sQuery(id+"F0.wireOp",EDGE,"E13.21.0"),sQuery(id+"F0.wireOp",EDGE,"E13.21.1"),sQuery(id+"F0.wireOp",EDGE,"E13.21.2"),sQuery(id+"F0.wireOp",EDGE,"E13.21.3"),sQuery(id+"F0.wireOp",EDGE,"E13.21.4"),sQuery(id+"F0.wireOp",EDGE,"E13.21.5"),sQuery(id+"F0.wireOp",EDGE,"E13.21.6"),sQuery(id+"F0.wireOp",EDGE,"E13.21.7"),sQuery(id+"F0.wireOp",EDGE,"E13.21.8"),sQuery(id+"F0.wireOp",EDGE,"E13.21.9"),sQuery(id+"F0.wireOp",EDGE,"E13.21.10"),sQuery(id+"F0.wireOp",EDGE,"E13.21.11"),sQuery(id+"F0.wireOp",EDGE,"E13.22.0"),sQuery(id+"F0.wireOp",EDGE,"E13.22.1"),sQuery(id+"F0.wireOp",EDGE,"E13.22.2"),sQuery(id+"F0.wireOp",EDGE,"E13.22.3"),sQuery(id+"F0.wireOp",EDGE,"E13.22.4"),sQuery(id+"F0.wireOp",EDGE,"E13.22.5"),sQuery(id+"F0.wireOp",EDGE,"E13.22.6"),sQuery(id+"F0.wireOp",EDGE,"E13.22.7"),sQuery(id+"F0.wireOp",EDGE,"E13.22.8"),sQuery(id+"F0.wireOp",EDGE,"E13.22.9"),sQuery(id+"F0.wireOp",EDGE,"E13.22.10"),sQuery(id+"F0.wireOp",EDGE,"E13.22.11"),sQuery(id+"F0.wireOp",EDGE,"E13.23.0"),sQuery(id+"F0.wireOp",EDGE,"E13.23.1"),sQuery(id+"F0.wireOp",EDGE,"E13.23.2"),sQuery(id+"F0.wireOp",EDGE,"E13.23.3"),sQuery(id+"F0.wireOp",EDGE,"E13.23.4"),sQuery(id+"F0.wireOp",EDGE,"E13.23.5"),sQuery(id+"F0.wireOp",EDGE,"E13.23.6"),sQuery(id+"F0.wireOp",EDGE,"E13.23.7"),sQuery(id+"F0.wireOp",EDGE,"E13.23.8"),sQuery(id+"F0.wireOp",EDGE,"E13.23.9"),sQuery(id+"F0.wireOp",EDGE,"E13.23.10"),sQuery(id+"F0.wireOp",EDGE,"E13.23.11"),sQuery(id+"F0.wireOp",EDGE,"E13.24.0"),sQuery(id+"F0.wireOp",EDGE,"E13.24.1"),sQuery(id+"F0.wireOp",EDGE,"E13.24.2"),sQuery(id+"F0.wireOp",EDGE,"E13.24.3"),sQuery(id+"F0.wireOp",EDGE,"E13.24.4"),sQuery(id+"F0.wireOp",EDGE,"E13.24.5"),sQuery(id+"F0.wireOp",EDGE,"E13.24.6"),sQuery(id+"F0.wireOp",EDGE,"E13.24.7"),sQuery(id+"F0.wireOp",EDGE,"E13.24.8"),sQuery(id+"F0.wireOp",EDGE,"E13.24.9"),sQuery(id+"F0.wireOp",EDGE,"E13.24.10"),sQuery(id+"F0.wireOp",EDGE,"E13.24.11"),sQuery(id+"F0.wireOp",EDGE,"E13.25.0"),sQuery(id+"F0.wireOp",EDGE,"E13.25.1"),sQuery(id+"F0.wireOp",EDGE,"E13.25.2"),sQuery(id+"F0.wireOp",EDGE,"E13.25.3"),sQuery(id+"F0.wireOp",EDGE,"E13.25.4"),sQuery(id+"F0.wireOp",EDGE,"E13.25.5"),sQuery(id+"F0.wireOp",EDGE,"E13.25.6"),sQuery(id+"F0.wireOp",EDGE,"E13.25.7"),sQuery(id+"F0.wireOp",EDGE,"E13.25.8"),sQuery(id+"F0.wireOp",EDGE,"E13.25.9"),sQuery(id+"F0.wireOp",EDGE,"E13.25.10"),sQuery(id+"F0.wireOp",EDGE,"E13.25.11"),sQuery(id+"F0.wireOp",EDGE,"E13.26.0"),sQuery(id+"F0.wireOp",EDGE,"E13.26.1"),sQuery(id+"F0.wireOp",EDGE,"E13.26.2"),sQuery(id+"F0.wireOp",EDGE,"E13.26.3"),sQuery(id+"F0.wireOp",EDGE,"E13.26.4"),sQuery(id+"F0.wireOp",EDGE,"E13.26.5"),sQuery(id+"F0.wireOp",EDGE,"E13.26.6"),sQuery(id+"F0.wireOp",EDGE,"E13.26.7"),sQuery(id+"F0.wireOp",EDGE,"E13.26.8"),sQuery(id+"F0.wireOp",EDGE,"E13.26.9"),sQuery(id+"F0.wireOp",EDGE,"E13.26.10"),sQuery(id+"F0.wireOp",EDGE,"E13.26.11"),sQuery(id+"F0.wireOp",EDGE,"E13.27.0"),sQuery(id+"F0.wireOp",EDGE,"E13.27.1"),sQuery(id+"F0.wireOp",EDGE,"E13.27.2"),sQuery(id+"F0.wireOp",EDGE,"E13.27.3"),sQuery(id+"F0.wireOp",EDGE,"E13.27.4"),sQuery(id+"F0.wireOp",EDGE,"E13.27.5"),sQuery(id+"F0.wireOp",EDGE,"E13.27.6"),sQuery(id+"F0.wireOp",EDGE,"E13.27.7"),sQuery(id+"F0.wireOp",EDGE,"E13.27.8"),sQuery(id+"F0.wireOp",EDGE,"E13.27.9"),sQuery(id+"F0.wireOp",EDGE,"E13.27.10"),sQuery(id+"F0.wireOp",EDGE,"E13.27.11"),sQuery(id+"F0.wireOp",EDGE,"E13.28.0"),sQuery(id+"F0.wireOp",EDGE,"E13.28.1"),sQuery(id+"F0.wireOp",EDGE,"E13.28.2"),sQuery(id+"F0.wireOp",EDGE,"E13.28.3"),sQuery(id+"F0.wireOp",EDGE,"E13.28.4"),sQuery(id+"F0.wireOp",EDGE,"E13.28.5"),sQuery(id+"F0.wireOp",EDGE,"E13.28.6"),sQuery(id+"F0.wireOp",EDGE,"E13.28.7"),sQuery(id+"F0.wireOp",EDGE,"E13.28.8"),sQuery(id+"F0.wireOp",EDGE,"E13.28.9"),sQuery(id+"F0.wireOp",EDGE,"E13.28.10"),sQuery(id+"F0.wireOp",EDGE,"E13.28.11"),sQuery(id+"F0.wireOp",EDGE,"E13.29.0"),sQuery(id+"F0.wireOp",EDGE,"E13.29.1"),sQuery(id+"F0.wireOp",EDGE,"E13.29.2"),sQuery(id+"F0.wireOp",EDGE,"E13.29.3"),sQuery(id+"F0.wireOp",EDGE,"E13.29.4"),sQuery(id+"F0.wireOp",EDGE,"E13.29.5"),sQuery(id+"F0.wireOp",EDGE,"E13.29.6"),sQuery(id+"F0.wireOp",EDGE,"E13.29.7"),sQuery(id+"F0.wireOp",EDGE,"E13.29.8"),sQuery(id+"F0.wireOp",EDGE,"E13.29.9"),sQuery(id+"F0.wireOp",EDGE,"E13.29.10"),sQuery(id+"F0.wireOp",EDGE,"E13.29.11"),sQuery(id+"F0.wireOp",EDGE,"E13.30.0"),sQuery(id+"F0.wireOp",EDGE,"E13.30.1"),sQuery(id+"F0.wireOp",EDGE,"E13.30.2"),sQuery(id+"F0.wireOp",EDGE,"E13.30.3"),sQuery(id+"F0.wireOp",EDGE,"E13.30.4"),sQuery(id+"F0.wireOp",EDGE,"E13.30.5"),sQuery(id+"F0.wireOp",EDGE,"E13.30.6"),sQuery(id+"F0.wireOp",EDGE,"E13.30.7"),sQuery(id+"F0.wireOp",EDGE,"E13.30.8"),sQuery(id+"F0.wireOp",EDGE,"E13.30.9"),sQuery(id+"F0.wireOp",EDGE,"E13.30.10"),sQuery(id+"F0.wireOp",EDGE,"E13.30.11"),sQuery(id+"F0.wireOp",EDGE,"E13.31.0"),sQuery(id+"F0.wireOp",EDGE,"E13.31.1"),sQuery(id+"F0.wireOp",EDGE,"E13.31.2"),sQuery(id+"F0.wireOp",EDGE,"E13.31.3"),sQuery(id+"F0.wireOp",EDGE,"E13.31.4"),sQuery(id+"F0.wireOp",EDGE,"E13.31.5"),sQuery(id+"F0.wireOp",EDGE,"E13.31.6"),sQuery(id+"F0.wireOp",EDGE,"E13.31.7"),sQuery(id+"F0.wireOp",EDGE,"E13.31.8"),sQuery(id+"F0.wireOp",EDGE,"E13.31.9"),sQuery(id+"F0.wireOp",EDGE,"E13.31.10"),sQuery(id+"F0.wireOp",EDGE,"E13.31.11"),sQuery(id+"F0.wireOp",EDGE,"E13.32.0"),sQuery(id+"F0.wireOp",EDGE,"E13.32.1"),sQuery(id+"F0.wireOp",EDGE,"E13.32.2"),sQuery(id+"F0.wireOp",EDGE,"E13.32.3"),sQuery(id+"F0.wireOp",EDGE,"E13.32.4"),sQuery(id+"F0.wireOp",EDGE,"E13.32.5"),sQuery(id+"F0.wireOp",EDGE,"E13.32.6"),sQuery(id+"F0.wireOp",EDGE,"E13.32.7"),sQuery(id+"F0.wireOp",EDGE,"E13.32.8"),sQuery(id+"F0.wireOp",EDGE,"E13.32.9"),sQuery(id+"F0.wireOp",EDGE,"E13.32.10"),sQuery(id+"F0.wireOp",EDGE,"E13.32.11"),sQuery(id+"F0.wireOp",EDGE,"E13.33.0"),sQuery(id+"F0.wireOp",EDGE,"E13.33.1"),sQuery(id+"F0.wireOp",EDGE,"E13.33.2"),sQuery(id+"F0.wireOp",EDGE,"E13.33.3"),sQuery(id+"F0.wireOp",EDGE,"E13.33.4"),sQuery(id+"F0.wireOp",EDGE,"E13.33.5"),sQuery(id+"F0.wireOp",EDGE,"E13.33.6"),sQuery(id+"F0.wireOp",EDGE,"E13.33.7"),sQuery(id+"F0.wireOp",EDGE,"E13.33.8"),sQuery(id+"F0.wireOp",EDGE,"E13.33.9"),sQuery(id+"F0.wireOp",EDGE,"E13.33.10"),sQuery(id+"F0.wireOp",EDGE,"E13.33.11"),sQuery(id+"F0.wireOp",EDGE,"E13.34.0"),sQuery(id+"F0.wireOp",EDGE,"E13.34.1"),sQuery(id+"F0.wireOp",EDGE,"E13.34.2"),sQuery(id+"F0.wireOp",EDGE,"E13.34.3"),sQuery(id+"F0.wireOp",EDGE,"E13.34.4"),sQuery(id+"F0.wireOp",EDGE,"E13.34.5"),sQuery(id+"F0.wireOp",EDGE,"E13.34.6"),sQuery(id+"F0.wireOp",EDGE,"E13.34.7"),sQuery(id+"F0.wireOp",EDGE,"E13.34.8"),sQuery(id+"F0.wireOp",EDGE,"E13.34.9"),sQuery(id+"F0.wireOp",EDGE,"E13.34.10"),sQuery(id+"F0.wireOp",EDGE,"E13.34.11"),sQuery(id+"F0.wireOp",EDGE,"E13.35.0"),sQuery(id+"F0.wireOp",EDGE,"E13.35.1"),sQuery(id+"F0.wireOp",EDGE,"E13.35.2"),sQuery(id+"F0.wireOp",EDGE,"E13.35.3"),sQuery(id+"F0.wireOp",EDGE,"E13.35.4"),sQuery(id+"F0.wireOp",EDGE,"E13.35.5"),sQuery(id+"F0.wireOp",EDGE,"E13.35.6"),sQuery(id+"F0.wireOp",EDGE,"E13.35.7"),sQuery(id+"F0.wireOp",EDGE,"E13.35.8"),sQuery(id+"F0.wireOp",EDGE,"E13.35.9"),sQuery(id+"F0.wireOp",EDGE,"E13.35.10"),sQuery(id+"F0.wireOp",EDGE,"E13.35.11"),sQuery(id+"F0.wireOp",EDGE,"E14.trimOffspring"),sQuery(id+"F0.wireOp",EDGE,"E15.trimOffspring"),sQuery(id+"F0.wireOp",EDGE,"E16.trimOffspring"),sQuery(id+"F0.wireOp",EDGE,"E17.trimOffspring"),sQuery(id+"F0.wireOp",EDGE,"E18.trimOffspring"),sQuery(id+"F0.wireOp",EDGE,"E19.trimOffspring"),sQuery(id+"F0.wireOp",EDGE,"E20.trimOffspring"),sQuery(id+"F0.wireOp",EDGE,"E21.trimOffspring"),sQuery(id+"F0.wireOp",EDGE,"E22.trimOffspring"),sQuery(id+"F0.wireOp",EDGE,"E23.trimOffspring"),sQuery(id+"F0.wireOp",EDGE,"E24.trimOffspring"),sQuery(id+"F0.wireOp",EDGE,"E25.trimOffspring"),sQuery(id+"F0.wireOp",EDGE,"E26.trimOffspring"),sQuery(id+"F0.wireOp",EDGE,"E27.trimOffspring"),sQuery(id+"F0.wireOp",EDGE,"E28.trimOffspring"),sQuery(id+"F0.wireOp",EDGE,"E29.trimOffspring"),sQuery(id+"F0.wireOp",EDGE,"E30.trimOffspring"),sQuery(id+"F0.wireOp",EDGE,"E31.trimOffspring"),sQuery(id+"F0.wireOp",EDGE,"E32.trimOffspring"),sQuery(id+"F0.wireOp",EDGE,"E33.trimOffspring"),sQuery(id+"F0.wireOp",EDGE,"E34.trimOffspring"),sQuery(id+"F0.wireOp",EDGE,"E35.trimOffspring"),sQuery(id+"F0.wireOp",EDGE,"E36.trimOffspring"),sQuery(id+"F0.wireOp",EDGE,"E37.trimOffspring"),sQuery(id+"F0.wireOp",EDGE,"E38.trimOffspring"),sQuery(id+"F0.wireOp",EDGE,"E39.trimOffspring"),sQuery(id+"F0.wireOp",EDGE,"E40.trimOffspring"),sQuery(id+"F0.wireOp",EDGE,"E41.trimOffspring"),sQuery(id+"F0.wireOp",EDGE,"E42.trimOffspring"),sQuery(id+"F0.wireOp",EDGE,"E43.trimOffspring"),sQuery(id+"F0.wireOp",EDGE,"E44.trimOffspring"),sQuery(id+"F0.wireOp",EDGE,"E45.trimOffspring"),sQuery(id+"F0.wireOp",EDGE,"E46.trimOffspring"),sQuery(id+"F0.wireOp",EDGE,"E47.trimOffspring"),sQuery(id+"F0.wireOp",EDGE,"E48.trimOffspring")])],"isStart":false});
            var sketch = newSketch(context, id + "F2", { "sketchPlane" : qUnion([Q0])});
            skCircle(sketch, "E49", {"center": v(0, 0) * mm, "radius": 3.18 * mm});
            skSolve(sketch);
        }
        {
            var Q0;
            Q0 = qSketchRegion(id + "F2", true);
            extrude(context, id + "F3", {"entities" : qUnion([Q0]), "operationType" : NewBodyOperationType.REMOVE, "oppositeDirection" : true, "depth" : 25.4 * mm});
        }
        {
            var Q0;
            Q0=makeQuery(id+"F1.opExtrude","CAP_FACE",FACE,{"disambiguationData":[OSD([sQuery(id+"F0.wireOp",EDGE,"E0"),sQuery(id+"F0.wireOp",EDGE,"E1.trimOffspring"),sQuery(id+"F0.wireOp",EDGE,"E2"),sQuery(id+"F0.wireOp",EDGE,"E3"),sQuery(id+"F0.wireOp",EDGE,"E4.MirrorCS"),sQuery(id+"F0.wireOp",EDGE,"E5.MirrorCS"),sQuery(id+"F0.wireOp",EDGE,"E6.MirrorCS"),sQuery(id+"F0.wireOp",EDGE,"E7.filletArc"),sQuery(id+"F0.wireOp",EDGE,"E8.filletArc"),sQuery(id+"F0.wireOp",EDGE,"E9.filletArc"),sQuery(id+"F0.wireOp",EDGE,"E10.filletArc"),sQuery(id+"F0.wireOp",EDGE,"E11.filletArc"),sQuery(id+"F0.wireOp",EDGE,"E12.filletArc"),sQuery(id+"F0.wireOp",EDGE,"E13.1.0"),sQuery(id+"F0.wireOp",EDGE,"E13.1.1"),sQuery(id+"F0.wireOp",EDGE,"E13.1.2"),sQuery(id+"F0.wireOp",EDGE,"E13.1.3"),sQuery(id+"F0.wireOp",EDGE,"E13.1.4"),sQuery(id+"F0.wireOp",EDGE,"E13.1.5"),sQuery(id+"F0.wireOp",EDGE,"E13.1.6"),sQuery(id+"F0.wireOp",EDGE,"E13.1.7"),sQuery(id+"F0.wireOp",EDGE,"E13.1.8"),sQuery(id+"F0.wireOp",EDGE,"E13.1.9"),sQuery(id+"F0.wireOp",EDGE,"E13.1.10"),sQuery(id+"F0.wireOp",EDGE,"E13.1.11"),sQuery(id+"F0.wireOp",EDGE,"E13.2.0"),sQuery(id+"F0.wireOp",EDGE,"E13.2.1"),sQuery(id+"F0.wireOp",EDGE,"E13.2.2"),sQuery(id+"F0.wireOp",EDGE,"E13.2.3"),sQuery(id+"F0.wireOp",EDGE,"E13.2.4"),sQuery(id+"F0.wireOp",EDGE,"E13.2.5"),sQuery(id+"F0.wireOp",EDGE,"E13.2.6"),sQuery(id+"F0.wireOp",EDGE,"E13.2.7"),sQuery(id+"F0.wireOp",EDGE,"E13.2.8"),sQuery(id+"F0.wireOp",EDGE,"E13.2.9"),sQuery(id+"F0.wireOp",EDGE,"E13.2.10"),sQuery(id+"F0.wireOp",EDGE,"E13.2.11"),sQuery(id+"F0.wireOp",EDGE,"E13.3.0"),sQuery(id+"F0.wireOp",EDGE,"E13.3.1"),sQuery(id+"F0.wireOp",EDGE,"E13.3.2"),sQuery(id+"F0.wireOp",EDGE,"E13.3.3"),sQuery(id+"F0.wireOp",EDGE,"E13.3.4"),sQuery(id+"F0.wireOp",EDGE,"E13.3.5"),sQuery(id+"F0.wireOp",EDGE,"E13.3.6"),sQuery(id+"F0.wireOp",EDGE,"E13.3.7"),sQuery(id+"F0.wireOp",EDGE,"E13.3.8"),sQuery(id+"F0.wireOp",EDGE,"E13.3.9"),sQuery(id+"F0.wireOp",EDGE,"E13.3.10"),sQuery(id+"F0.wireOp",EDGE,"E13.3.11"),sQuery(id+"F0.wireOp",EDGE,"E13.4.0"),sQuery(id+"F0.wireOp",EDGE,"E13.4.1"),sQuery(id+"F0.wireOp",EDGE,"E13.4.2"),sQuery(id+"F0.wireOp",EDGE,"E13.4.3"),sQuery(id+"F0.wireOp",EDGE,"E13.4.4"),sQuery(id+"F0.wireOp",EDGE,"E13.4.5"),sQuery(id+"F0.wireOp",EDGE,"E13.4.6"),sQuery(id+"F0.wireOp",EDGE,"E13.4.7"),sQuery(id+"F0.wireOp",EDGE,"E13.4.8"),sQuery(id+"F0.wireOp",EDGE,"E13.4.9"),sQuery(id+"F0.wireOp",EDGE,"E13.4.10"),sQuery(id+"F0.wireOp",EDGE,"E13.4.11"),sQuery(id+"F0.wireOp",EDGE,"E13.5.0"),sQuery(id+"F0.wireOp",EDGE,"E13.5.1"),sQuery(id+"F0.wireOp",EDGE,"E13.5.2"),sQuery(id+"F0.wireOp",EDGE,"E13.5.3"),sQuery(id+"F0.wireOp",EDGE,"E13.5.4"),sQuery(id+"F0.wireOp",EDGE,"E13.5.5"),sQuery(id+"F0.wireOp",EDGE,"E13.5.6"),sQuery(id+"F0.wireOp",EDGE,"E13.5.7"),sQuery(id+"F0.wireOp",EDGE,"E13.5.8"),sQuery(id+"F0.wireOp",EDGE,"E13.5.9"),sQuery(id+"F0.wireOp",EDGE,"E13.5.10"),sQuery(id+"F0.wireOp",EDGE,"E13.5.11"),sQuery(id+"F0.wireOp",EDGE,"E13.6.0"),sQuery(id+"F0.wireOp",EDGE,"E13.6.1"),sQuery(id+"F0.wireOp",EDGE,"E13.6.2"),sQuery(id+"F0.wireOp",EDGE,"E13.6.3"),sQuery(id+"F0.wireOp",EDGE,"E13.6.4"),sQuery(id+"F0.wireOp",EDGE,"E13.6.5"),sQuery(id+"F0.wireOp",EDGE,"E13.6.6"),sQuery(id+"F0.wireOp",EDGE,"E13.6.7"),sQuery(id+"F0.wireOp",EDGE,"E13.6.8"),sQuery(id+"F0.wireOp",EDGE,"E13.6.9"),sQuery(id+"F0.wireOp",EDGE,"E13.6.10"),sQuery(id+"F0.wireOp",EDGE,"E13.6.11"),sQuery(id+"F0.wireOp",EDGE,"E13.7.0"),sQuery(id+"F0.wireOp",EDGE,"E13.7.1"),sQuery(id+"F0.wireOp",EDGE,"E13.7.2"),sQuery(id+"F0.wireOp",EDGE,"E13.7.3"),sQuery(id+"F0.wireOp",EDGE,"E13.7.4"),sQuery(id+"F0.wireOp",EDGE,"E13.7.5"),sQuery(id+"F0.wireOp",EDGE,"E13.7.6"),sQuery(id+"F0.wireOp",EDGE,"E13.7.7"),sQuery(id+"F0.wireOp",EDGE,"E13.7.8"),sQuery(id+"F0.wireOp",EDGE,"E13.7.9"),sQuery(id+"F0.wireOp",EDGE,"E13.7.10"),sQuery(id+"F0.wireOp",EDGE,"E13.7.11"),sQuery(id+"F0.wireOp",EDGE,"E13.8.0"),sQuery(id+"F0.wireOp",EDGE,"E13.8.1"),sQuery(id+"F0.wireOp",EDGE,"E13.8.2"),sQuery(id+"F0.wireOp",EDGE,"E13.8.3"),sQuery(id+"F0.wireOp",EDGE,"E13.8.4"),sQuery(id+"F0.wireOp",EDGE,"E13.8.5"),sQuery(id+"F0.wireOp",EDGE,"E13.8.6"),sQuery(id+"F0.wireOp",EDGE,"E13.8.7"),sQuery(id+"F0.wireOp",EDGE,"E13.8.8"),sQuery(id+"F0.wireOp",EDGE,"E13.8.9"),sQuery(id+"F0.wireOp",EDGE,"E13.8.10"),sQuery(id+"F0.wireOp",EDGE,"E13.8.11"),sQuery(id+"F0.wireOp",EDGE,"E13.9.0"),sQuery(id+"F0.wireOp",EDGE,"E13.9.1"),sQuery(id+"F0.wireOp",EDGE,"E13.9.2"),sQuery(id+"F0.wireOp",EDGE,"E13.9.3"),sQuery(id+"F0.wireOp",EDGE,"E13.9.4"),sQuery(id+"F0.wireOp",EDGE,"E13.9.5"),sQuery(id+"F0.wireOp",EDGE,"E13.9.6"),sQuery(id+"F0.wireOp",EDGE,"E13.9.7"),sQuery(id+"F0.wireOp",EDGE,"E13.9.8"),sQuery(id+"F0.wireOp",EDGE,"E13.9.9"),sQuery(id+"F0.wireOp",EDGE,"E13.9.10"),sQuery(id+"F0.wireOp",EDGE,"E13.9.11"),sQuery(id+"F0.wireOp",EDGE,"E13.10.0"),sQuery(id+"F0.wireOp",EDGE,"E13.10.1"),sQuery(id+"F0.wireOp",EDGE,"E13.10.2"),sQuery(id+"F0.wireOp",EDGE,"E13.10.3"),sQuery(id+"F0.wireOp",EDGE,"E13.10.4"),sQuery(id+"F0.wireOp",EDGE,"E13.10.5"),sQuery(id+"F0.wireOp",EDGE,"E13.10.6"),sQuery(id+"F0.wireOp",EDGE,"E13.10.7"),sQuery(id+"F0.wireOp",EDGE,"E13.10.8"),sQuery(id+"F0.wireOp",EDGE,"E13.10.9"),sQuery(id+"F0.wireOp",EDGE,"E13.10.10"),sQuery(id+"F0.wireOp",EDGE,"E13.10.11"),sQuery(id+"F0.wireOp",EDGE,"E13.11.0"),sQuery(id+"F0.wireOp",EDGE,"E13.11.1"),sQuery(id+"F0.wireOp",EDGE,"E13.11.2"),sQuery(id+"F0.wireOp",EDGE,"E13.11.3"),sQuery(id+"F0.wireOp",EDGE,"E13.11.4"),sQuery(id+"F0.wireOp",EDGE,"E13.11.5"),sQuery(id+"F0.wireOp",EDGE,"E13.11.6"),sQuery(id+"F0.wireOp",EDGE,"E13.11.7"),sQuery(id+"F0.wireOp",EDGE,"E13.11.8"),sQuery(id+"F0.wireOp",EDGE,"E13.11.9"),sQuery(id+"F0.wireOp",EDGE,"E13.11.10"),sQuery(id+"F0.wireOp",EDGE,"E13.11.11"),sQuery(id+"F0.wireOp",EDGE,"E13.12.0"),sQuery(id+"F0.wireOp",EDGE,"E13.12.1"),sQuery(id+"F0.wireOp",EDGE,"E13.12.2"),sQuery(id+"F0.wireOp",EDGE,"E13.12.3"),sQuery(id+"F0.wireOp",EDGE,"E13.12.4"),sQuery(id+"F0.wireOp",EDGE,"E13.12.5"),sQuery(id+"F0.wireOp",EDGE,"E13.12.6"),sQuery(id+"F0.wireOp",EDGE,"E13.12.7"),sQuery(id+"F0.wireOp",EDGE,"E13.12.8"),sQuery(id+"F0.wireOp",EDGE,"E13.12.9"),sQuery(id+"F0.wireOp",EDGE,"E13.12.10"),sQuery(id+"F0.wireOp",EDGE,"E13.12.11"),sQuery(id+"F0.wireOp",EDGE,"E13.13.0"),sQuery(id+"F0.wireOp",EDGE,"E13.13.1"),sQuery(id+"F0.wireOp",EDGE,"E13.13.2"),sQuery(id+"F0.wireOp",EDGE,"E13.13.3"),sQuery(id+"F0.wireOp",EDGE,"E13.13.4"),sQuery(id+"F0.wireOp",EDGE,"E13.13.5"),sQuery(id+"F0.wireOp",EDGE,"E13.13.6"),sQuery(id+"F0.wireOp",EDGE,"E13.13.7"),sQuery(id+"F0.wireOp",EDGE,"E13.13.8"),sQuery(id+"F0.wireOp",EDGE,"E13.13.9"),sQuery(id+"F0.wireOp",EDGE,"E13.13.10"),sQuery(id+"F0.wireOp",EDGE,"E13.13.11"),sQuery(id+"F0.wireOp",EDGE,"E13.14.0"),sQuery(id+"F0.wireOp",EDGE,"E13.14.1"),sQuery(id+"F0.wireOp",EDGE,"E13.14.2"),sQuery(id+"F0.wireOp",EDGE,"E13.14.3"),sQuery(id+"F0.wireOp",EDGE,"E13.14.4"),sQuery(id+"F0.wireOp",EDGE,"E13.14.5"),sQuery(id+"F0.wireOp",EDGE,"E13.14.6"),sQuery(id+"F0.wireOp",EDGE,"E13.14.7"),sQuery(id+"F0.wireOp",EDGE,"E13.14.8"),sQuery(id+"F0.wireOp",EDGE,"E13.14.9"),sQuery(id+"F0.wireOp",EDGE,"E13.14.10"),sQuery(id+"F0.wireOp",EDGE,"E13.14.11"),sQuery(id+"F0.wireOp",EDGE,"E13.15.0"),sQuery(id+"F0.wireOp",EDGE,"E13.15.1"),sQuery(id+"F0.wireOp",EDGE,"E13.15.2"),sQuery(id+"F0.wireOp",EDGE,"E13.15.3"),sQuery(id+"F0.wireOp",EDGE,"E13.15.4"),sQuery(id+"F0.wireOp",EDGE,"E13.15.5"),sQuery(id+"F0.wireOp",EDGE,"E13.15.6"),sQuery(id+"F0.wireOp",EDGE,"E13.15.7"),sQuery(id+"F0.wireOp",EDGE,"E13.15.8"),sQuery(id+"F0.wireOp",EDGE,"E13.15.9"),sQuery(id+"F0.wireOp",EDGE,"E13.15.10"),sQuery(id+"F0.wireOp",EDGE,"E13.15.11"),sQuery(id+"F0.wireOp",EDGE,"E13.16.0"),sQuery(id+"F0.wireOp",EDGE,"E13.16.1"),sQuery(id+"F0.wireOp",EDGE,"E13.16.2"),sQuery(id+"F0.wireOp",EDGE,"E13.16.3"),sQuery(id+"F0.wireOp",EDGE,"E13.16.4"),sQuery(id+"F0.wireOp",EDGE,"E13.16.5"),sQuery(id+"F0.wireOp",EDGE,"E13.16.6"),sQuery(id+"F0.wireOp",EDGE,"E13.16.7"),sQuery(id+"F0.wireOp",EDGE,"E13.16.8"),sQuery(id+"F0.wireOp",EDGE,"E13.16.9"),sQuery(id+"F0.wireOp",EDGE,"E13.16.10"),sQuery(id+"F0.wireOp",EDGE,"E13.16.11"),sQuery(id+"F0.wireOp",EDGE,"E13.17.0"),sQuery(id+"F0.wireOp",EDGE,"E13.17.1"),sQuery(id+"F0.wireOp",EDGE,"E13.17.2"),sQuery(id+"F0.wireOp",EDGE,"E13.17.3"),sQuery(id+"F0.wireOp",EDGE,"E13.17.4"),sQuery(id+"F0.wireOp",EDGE,"E13.17.5"),sQuery(id+"F0.wireOp",EDGE,"E13.17.6"),sQuery(id+"F0.wireOp",EDGE,"E13.17.7"),sQuery(id+"F0.wireOp",EDGE,"E13.17.8"),sQuery(id+"F0.wireOp",EDGE,"E13.17.9"),sQuery(id+"F0.wireOp",EDGE,"E13.17.10"),sQuery(id+"F0.wireOp",EDGE,"E13.17.11"),sQuery(id+"F0.wireOp",EDGE,"E13.18.0"),sQuery(id+"F0.wireOp",EDGE,"E13.18.1"),sQuery(id+"F0.wireOp",EDGE,"E13.18.2"),sQuery(id+"F0.wireOp",EDGE,"E13.18.3"),sQuery(id+"F0.wireOp",EDGE,"E13.18.4"),sQuery(id+"F0.wireOp",EDGE,"E13.18.5"),sQuery(id+"F0.wireOp",EDGE,"E13.18.6"),sQuery(id+"F0.wireOp",EDGE,"E13.18.7"),sQuery(id+"F0.wireOp",EDGE,"E13.18.8"),sQuery(id+"F0.wireOp",EDGE,"E13.18.9"),sQuery(id+"F0.wireOp",EDGE,"E13.18.10"),sQuery(id+"F0.wireOp",EDGE,"E13.18.11"),sQuery(id+"F0.wireOp",EDGE,"E13.19.0"),sQuery(id+"F0.wireOp",EDGE,"E13.19.1"),sQuery(id+"F0.wireOp",EDGE,"E13.19.2"),sQuery(id+"F0.wireOp",EDGE,"E13.19.3"),sQuery(id+"F0.wireOp",EDGE,"E13.19.4"),sQuery(id+"F0.wireOp",EDGE,"E13.19.5"),sQuery(id+"F0.wireOp",EDGE,"E13.19.6"),sQuery(id+"F0.wireOp",EDGE,"E13.19.7"),sQuery(id+"F0.wireOp",EDGE,"E13.19.8"),sQuery(id+"F0.wireOp",EDGE,"E13.19.9"),sQuery(id+"F0.wireOp",EDGE,"E13.19.10"),sQuery(id+"F0.wireOp",EDGE,"E13.19.11"),sQuery(id+"F0.wireOp",EDGE,"E13.20.0"),sQuery(id+"F0.wireOp",EDGE,"E13.20.1"),sQuery(id+"F0.wireOp",EDGE,"E13.20.2"),sQuery(id+"F0.wireOp",EDGE,"E13.20.3"),sQuery(id+"F0.wireOp",EDGE,"E13.20.4"),sQuery(id+"F0.wireOp",EDGE,"E13.20.5"),sQuery(id+"F0.wireOp",EDGE,"E13.20.6"),sQuery(id+"F0.wireOp",EDGE,"E13.20.7"),sQuery(id+"F0.wireOp",EDGE,"E13.20.8"),sQuery(id+"F0.wireOp",EDGE,"E13.20.9"),sQuery(id+"F0.wireOp",EDGE,"E13.20.10"),sQuery(id+"F0.wireOp",EDGE,"E13.20.11"),sQuery(id+"F0.wireOp",EDGE,"E13.21.0"),sQuery(id+"F0.wireOp",EDGE,"E13.21.1"),sQuery(id+"F0.wireOp",EDGE,"E13.21.2"),sQuery(id+"F0.wireOp",EDGE,"E13.21.3"),sQuery(id+"F0.wireOp",EDGE,"E13.21.4"),sQuery(id+"F0.wireOp",EDGE,"E13.21.5"),sQuery(id+"F0.wireOp",EDGE,"E13.21.6"),sQuery(id+"F0.wireOp",EDGE,"E13.21.7"),sQuery(id+"F0.wireOp",EDGE,"E13.21.8"),sQuery(id+"F0.wireOp",EDGE,"E13.21.9"),sQuery(id+"F0.wireOp",EDGE,"E13.21.10"),sQuery(id+"F0.wireOp",EDGE,"E13.21.11"),sQuery(id+"F0.wireOp",EDGE,"E13.22.0"),sQuery(id+"F0.wireOp",EDGE,"E13.22.1"),sQuery(id+"F0.wireOp",EDGE,"E13.22.2"),sQuery(id+"F0.wireOp",EDGE,"E13.22.3"),sQuery(id+"F0.wireOp",EDGE,"E13.22.4"),sQuery(id+"F0.wireOp",EDGE,"E13.22.5"),sQuery(id+"F0.wireOp",EDGE,"E13.22.6"),sQuery(id+"F0.wireOp",EDGE,"E13.22.7"),sQuery(id+"F0.wireOp",EDGE,"E13.22.8"),sQuery(id+"F0.wireOp",EDGE,"E13.22.9"),sQuery(id+"F0.wireOp",EDGE,"E13.22.10"),sQuery(id+"F0.wireOp",EDGE,"E13.22.11"),sQuery(id+"F0.wireOp",EDGE,"E13.23.0"),sQuery(id+"F0.wireOp",EDGE,"E13.23.1"),sQuery(id+"F0.wireOp",EDGE,"E13.23.2"),sQuery(id+"F0.wireOp",EDGE,"E13.23.3"),sQuery(id+"F0.wireOp",EDGE,"E13.23.4"),sQuery(id+"F0.wireOp",EDGE,"E13.23.5"),sQuery(id+"F0.wireOp",EDGE,"E13.23.6"),sQuery(id+"F0.wireOp",EDGE,"E13.23.7"),sQuery(id+"F0.wireOp",EDGE,"E13.23.8"),sQuery(id+"F0.wireOp",EDGE,"E13.23.9"),sQuery(id+"F0.wireOp",EDGE,"E13.23.10"),sQuery(id+"F0.wireOp",EDGE,"E13.23.11"),sQuery(id+"F0.wireOp",EDGE,"E13.24.0"),sQuery(id+"F0.wireOp",EDGE,"E13.24.1"),sQuery(id+"F0.wireOp",EDGE,"E13.24.2"),sQuery(id+"F0.wireOp",EDGE,"E13.24.3"),sQuery(id+"F0.wireOp",EDGE,"E13.24.4"),sQuery(id+"F0.wireOp",EDGE,"E13.24.5"),sQuery(id+"F0.wireOp",EDGE,"E13.24.6"),sQuery(id+"F0.wireOp",EDGE,"E13.24.7"),sQuery(id+"F0.wireOp",EDGE,"E13.24.8"),sQuery(id+"F0.wireOp",EDGE,"E13.24.9"),sQuery(id+"F0.wireOp",EDGE,"E13.24.10"),sQuery(id+"F0.wireOp",EDGE,"E13.24.11"),sQuery(id+"F0.wireOp",EDGE,"E13.25.0"),sQuery(id+"F0.wireOp",EDGE,"E13.25.1"),sQuery(id+"F0.wireOp",EDGE,"E13.25.2"),sQuery(id+"F0.wireOp",EDGE,"E13.25.3"),sQuery(id+"F0.wireOp",EDGE,"E13.25.4"),sQuery(id+"F0.wireOp",EDGE,"E13.25.5"),sQuery(id+"F0.wireOp",EDGE,"E13.25.6"),sQuery(id+"F0.wireOp",EDGE,"E13.25.7"),sQuery(id+"F0.wireOp",EDGE,"E13.25.8"),sQuery(id+"F0.wireOp",EDGE,"E13.25.9"),sQuery(id+"F0.wireOp",EDGE,"E13.25.10"),sQuery(id+"F0.wireOp",EDGE,"E13.25.11"),sQuery(id+"F0.wireOp",EDGE,"E13.26.0"),sQuery(id+"F0.wireOp",EDGE,"E13.26.1"),sQuery(id+"F0.wireOp",EDGE,"E13.26.2"),sQuery(id+"F0.wireOp",EDGE,"E13.26.3"),sQuery(id+"F0.wireOp",EDGE,"E13.26.4"),sQuery(id+"F0.wireOp",EDGE,"E13.26.5"),sQuery(id+"F0.wireOp",EDGE,"E13.26.6"),sQuery(id+"F0.wireOp",EDGE,"E13.26.7"),sQuery(id+"F0.wireOp",EDGE,"E13.26.8"),sQuery(id+"F0.wireOp",EDGE,"E13.26.9"),sQuery(id+"F0.wireOp",EDGE,"E13.26.10"),sQuery(id+"F0.wireOp",EDGE,"E13.26.11"),sQuery(id+"F0.wireOp",EDGE,"E13.27.0"),sQuery(id+"F0.wireOp",EDGE,"E13.27.1"),sQuery(id+"F0.wireOp",EDGE,"E13.27.2"),sQuery(id+"F0.wireOp",EDGE,"E13.27.3"),sQuery(id+"F0.wireOp",EDGE,"E13.27.4"),sQuery(id+"F0.wireOp",EDGE,"E13.27.5"),sQuery(id+"F0.wireOp",EDGE,"E13.27.6"),sQuery(id+"F0.wireOp",EDGE,"E13.27.7"),sQuery(id+"F0.wireOp",EDGE,"E13.27.8"),sQuery(id+"F0.wireOp",EDGE,"E13.27.9"),sQuery(id+"F0.wireOp",EDGE,"E13.27.10"),sQuery(id+"F0.wireOp",EDGE,"E13.27.11"),sQuery(id+"F0.wireOp",EDGE,"E13.28.0"),sQuery(id+"F0.wireOp",EDGE,"E13.28.1"),sQuery(id+"F0.wireOp",EDGE,"E13.28.2"),sQuery(id+"F0.wireOp",EDGE,"E13.28.3"),sQuery(id+"F0.wireOp",EDGE,"E13.28.4"),sQuery(id+"F0.wireOp",EDGE,"E13.28.5"),sQuery(id+"F0.wireOp",EDGE,"E13.28.6"),sQuery(id+"F0.wireOp",EDGE,"E13.28.7"),sQuery(id+"F0.wireOp",EDGE,"E13.28.8"),sQuery(id+"F0.wireOp",EDGE,"E13.28.9"),sQuery(id+"F0.wireOp",EDGE,"E13.28.10"),sQuery(id+"F0.wireOp",EDGE,"E13.28.11"),sQuery(id+"F0.wireOp",EDGE,"E13.29.0"),sQuery(id+"F0.wireOp",EDGE,"E13.29.1"),sQuery(id+"F0.wireOp",EDGE,"E13.29.2"),sQuery(id+"F0.wireOp",EDGE,"E13.29.3"),sQuery(id+"F0.wireOp",EDGE,"E13.29.4"),sQuery(id+"F0.wireOp",EDGE,"E13.29.5"),sQuery(id+"F0.wireOp",EDGE,"E13.29.6"),sQuery(id+"F0.wireOp",EDGE,"E13.29.7"),sQuery(id+"F0.wireOp",EDGE,"E13.29.8"),sQuery(id+"F0.wireOp",EDGE,"E13.29.9"),sQuery(id+"F0.wireOp",EDGE,"E13.29.10"),sQuery(id+"F0.wireOp",EDGE,"E13.29.11"),sQuery(id+"F0.wireOp",EDGE,"E13.30.0"),sQuery(id+"F0.wireOp",EDGE,"E13.30.1"),sQuery(id+"F0.wireOp",EDGE,"E13.30.2"),sQuery(id+"F0.wireOp",EDGE,"E13.30.3"),sQuery(id+"F0.wireOp",EDGE,"E13.30.4"),sQuery(id+"F0.wireOp",EDGE,"E13.30.5"),sQuery(id+"F0.wireOp",EDGE,"E13.30.6"),sQuery(id+"F0.wireOp",EDGE,"E13.30.7"),sQuery(id+"F0.wireOp",EDGE,"E13.30.8"),sQuery(id+"F0.wireOp",EDGE,"E13.30.9"),sQuery(id+"F0.wireOp",EDGE,"E13.30.10"),sQuery(id+"F0.wireOp",EDGE,"E13.30.11"),sQuery(id+"F0.wireOp",EDGE,"E13.31.0"),sQuery(id+"F0.wireOp",EDGE,"E13.31.1"),sQuery(id+"F0.wireOp",EDGE,"E13.31.2"),sQuery(id+"F0.wireOp",EDGE,"E13.31.3"),sQuery(id+"F0.wireOp",EDGE,"E13.31.4"),sQuery(id+"F0.wireOp",EDGE,"E13.31.5"),sQuery(id+"F0.wireOp",EDGE,"E13.31.6"),sQuery(id+"F0.wireOp",EDGE,"E13.31.7"),sQuery(id+"F0.wireOp",EDGE,"E13.31.8"),sQuery(id+"F0.wireOp",EDGE,"E13.31.9"),sQuery(id+"F0.wireOp",EDGE,"E13.31.10"),sQuery(id+"F0.wireOp",EDGE,"E13.31.11"),sQuery(id+"F0.wireOp",EDGE,"E13.32.0"),sQuery(id+"F0.wireOp",EDGE,"E13.32.1"),sQuery(id+"F0.wireOp",EDGE,"E13.32.2"),sQuery(id+"F0.wireOp",EDGE,"E13.32.3"),sQuery(id+"F0.wireOp",EDGE,"E13.32.4"),sQuery(id+"F0.wireOp",EDGE,"E13.32.5"),sQuery(id+"F0.wireOp",EDGE,"E13.32.6"),sQuery(id+"F0.wireOp",EDGE,"E13.32.7"),sQuery(id+"F0.wireOp",EDGE,"E13.32.8"),sQuery(id+"F0.wireOp",EDGE,"E13.32.9"),sQuery(id+"F0.wireOp",EDGE,"E13.32.10"),sQuery(id+"F0.wireOp",EDGE,"E13.32.11"),sQuery(id+"F0.wireOp",EDGE,"E13.33.0"),sQuery(id+"F0.wireOp",EDGE,"E13.33.1"),sQuery(id+"F0.wireOp",EDGE,"E13.33.2"),sQuery(id+"F0.wireOp",EDGE,"E13.33.3"),sQuery(id+"F0.wireOp",EDGE,"E13.33.4"),sQuery(id+"F0.wireOp",EDGE,"E13.33.5"),sQuery(id+"F0.wireOp",EDGE,"E13.33.6"),sQuery(id+"F0.wireOp",EDGE,"E13.33.7"),sQuery(id+"F0.wireOp",EDGE,"E13.33.8"),sQuery(id+"F0.wireOp",EDGE,"E13.33.9"),sQuery(id+"F0.wireOp",EDGE,"E13.33.10"),sQuery(id+"F0.wireOp",EDGE,"E13.33.11"),sQuery(id+"F0.wireOp",EDGE,"E13.34.0"),sQuery(id+"F0.wireOp",EDGE,"E13.34.1"),sQuery(id+"F0.wireOp",EDGE,"E13.34.2"),sQuery(id+"F0.wireOp",EDGE,"E13.34.3"),sQuery(id+"F0.wireOp",EDGE,"E13.34.4"),sQuery(id+"F0.wireOp",EDGE,"E13.34.5"),sQuery(id+"F0.wireOp",EDGE,"E13.34.6"),sQuery(id+"F0.wireOp",EDGE,"E13.34.7"),sQuery(id+"F0.wireOp",EDGE,"E13.34.8"),sQuery(id+"F0.wireOp",EDGE,"E13.34.9"),sQuery(id+"F0.wireOp",EDGE,"E13.34.10"),sQuery(id+"F0.wireOp",EDGE,"E13.34.11"),sQuery(id+"F0.wireOp",EDGE,"E13.35.0"),sQuery(id+"F0.wireOp",EDGE,"E13.35.1"),sQuery(id+"F0.wireOp",EDGE,"E13.35.2"),sQuery(id+"F0.wireOp",EDGE,"E13.35.3"),sQuery(id+"F0.wireOp",EDGE,"E13.35.4"),sQuery(id+"F0.wireOp",EDGE,"E13.35.5"),sQuery(id+"F0.wireOp",EDGE,"E13.35.6"),sQuery(id+"F0.wireOp",EDGE,"E13.35.7"),sQuery(id+"F0.wireOp",EDGE,"E13.35.8"),sQuery(id+"F0.wireOp",EDGE,"E13.35.9"),sQuery(id+"F0.wireOp",EDGE,"E13.35.10"),sQuery(id+"F0.wireOp",EDGE,"E13.35.11"),sQuery(id+"F0.wireOp",EDGE,"E14.trimOffspring"),sQuery(id+"F0.wireOp",EDGE,"E15.trimOffspring"),sQuery(id+"F0.wireOp",EDGE,"E16.trimOffspring"),sQuery(id+"F0.wireOp",EDGE,"E17.trimOffspring"),sQuery(id+"F0.wireOp",EDGE,"E18.trimOffspring"),sQuery(id+"F0.wireOp",EDGE,"E19.trimOffspring"),sQuery(id+"F0.wireOp",EDGE,"E20.trimOffspring"),sQuery(id+"F0.wireOp",EDGE,"E21.trimOffspring"),sQuery(id+"F0.wireOp",EDGE,"E22.trimOffspring"),sQuery(id+"F0.wireOp",EDGE,"E23.trimOffspring"),sQuery(id+"F0.wireOp",EDGE,"E24.trimOffspring"),sQuery(id+"F0.wireOp",EDGE,"E25.trimOffspring"),sQuery(id+"F0.wireOp",EDGE,"E26.trimOffspring"),sQuery(id+"F0.wireOp",EDGE,"E27.trimOffspring"),sQuery(id+"F0.wireOp",EDGE,"E28.trimOffspring"),sQuery(id+"F0.wireOp",EDGE,"E29.trimOffspring"),sQuery(id+"F0.wireOp",EDGE,"E30.trimOffspring"),sQuery(id+"F0.wireOp",EDGE,"E31.trimOffspring"),sQuery(id+"F0.wireOp",EDGE,"E32.trimOffspring"),sQuery(id+"F0.wireOp",EDGE,"E33.trimOffspring"),sQuery(id+"F0.wireOp",EDGE,"E34.trimOffspring"),sQuery(id+"F0.wireOp",EDGE,"E35.trimOffspring"),sQuery(id+"F0.wireOp",EDGE,"E36.trimOffspring"),sQuery(id+"F0.wireOp",EDGE,"E37.trimOffspring"),sQuery(id+"F0.wireOp",EDGE,"E38.trimOffspring"),sQuery(id+"F0.wireOp",EDGE,"E39.trimOffspring"),sQuery(id+"F0.wireOp",EDGE,"E40.trimOffspring"),sQuery(id+"F0.wireOp",EDGE,"E41.trimOffspring"),sQuery(id+"F0.wireOp",EDGE,"E42.trimOffspring"),sQuery(id+"F0.wireOp",EDGE,"E43.trimOffspring"),sQuery(id+"F0.wireOp",EDGE,"E44.trimOffspring"),sQuery(id+"F0.wireOp",EDGE,"E45.trimOffspring"),sQuery(id+"F0.wireOp",EDGE,"E46.trimOffspring"),sQuery(id+"F0.wireOp",EDGE,"E47.trimOffspring"),sQuery(id+"F0.wireOp",EDGE,"E48.trimOffspring")])],"isStart":false});
            shell(context, id + "F4", {"entities" : qUnion([Q0]), "thickness" : 6.35 * mm});
        }
        {
            var Q0;
            Q0=qCreatedBy(makeId("Right.planeOp"),FACE);
            cPlane(context, id + "F5", {"entities" : qUnion([Q0]), "cplaneType" : CPlaneType.OFFSET, "offset" : 9.52 * mm, "width" : 152.4 * mm, "height" : 152.4 * mm});
        }
        {
            var Q0;
            Q0=qCreatedBy(id+"F5.planeOp",FACE);
            var sketch = newSketch(context, id + "F6", { "sketchPlane" : qUnion([Q0])});
            skCircle(sketch, "E50", {"center": v(-9.53, 0) * mm, "radius": 1.13 * mm});
            skSolve(sketch);
        }
        {
            var Q0;
            Q0 = qSketchRegion(id + "F6", true);
            extrude(context, id + "F7", {"entities" : qUnion([Q0]), "operationType" : NewBodyOperationType.REMOVE, "oppositeDirection" : true, "depth" : 9.52 * mm});
        }
    });
